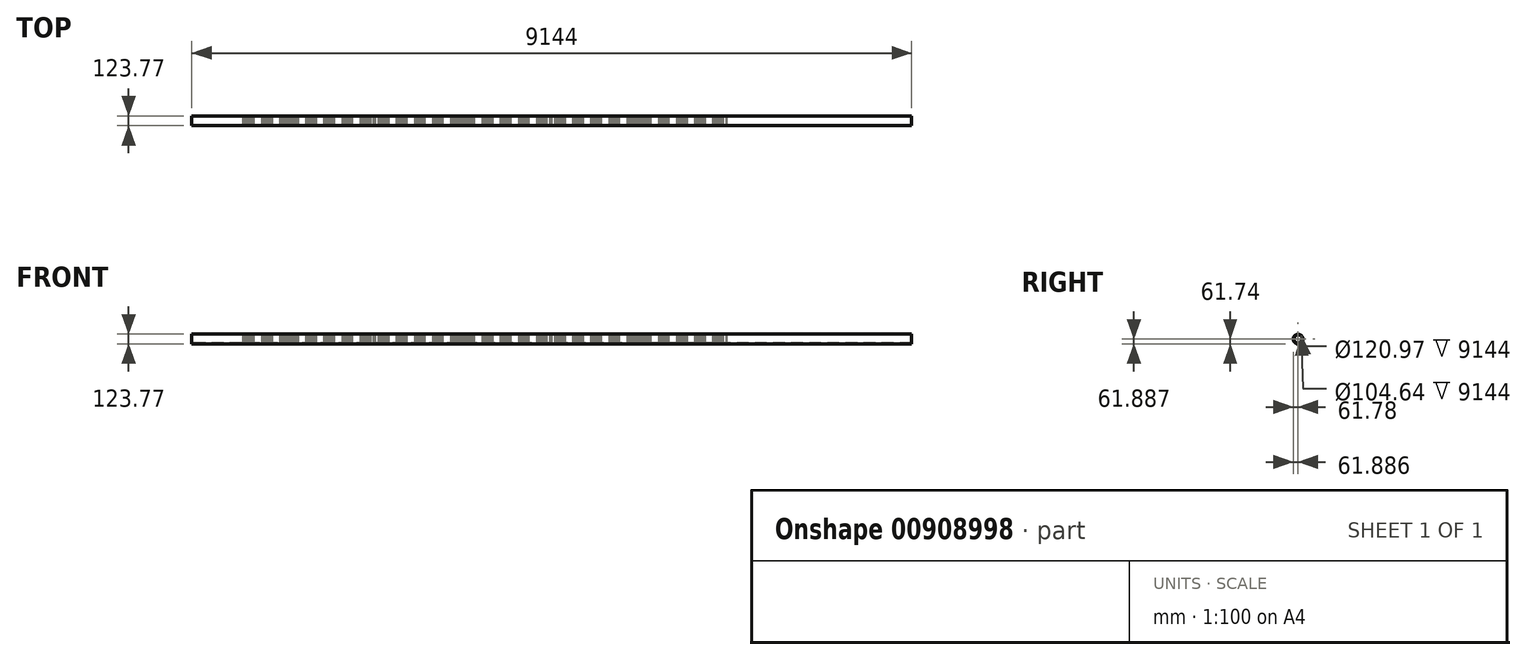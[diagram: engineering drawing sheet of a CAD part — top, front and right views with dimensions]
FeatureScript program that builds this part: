
annotation { "Feature Type Name" : "Feature", "Feature Type Description" : "" }
export const myFeature = defineFeature(function(context is Context, id is Id, definition is map)
    precondition{}
    {
        {
            var Q0;
            Q0=qCreatedBy(makeId("Right.planeOp"),FACE);
            var sketch = newSketch(context, id + "F0", { "sketchPlane" : qUnion([Q0])});
            skCircle(sketch, "E0", {"center": v(0, 0) * mm, "radius": 57.14 * mm});
            skCircle(sketch, "E1", {"center": v(0, 0) * mm, "radius": 52.32 * mm});
            skSolve(sketch);
        }
        {
            var Q0;
            Q0=qCreatedBy(makeId("Right.planeOp"),FACE);
            var sketch = newSketch(context, id + "F1", { "sketchPlane" : qUnion([Q0])});
            skLineSegment(sketch, "E2", {"start": v(57.25, 0) * mm, "end": v(57.25, 4.5) * mm});
            skLineSegment(sketch, "E3", {"start": v(57.25, 4.5) * mm, "end": v(59.26, 4.5) * mm});
            skLineSegment(sketch, "E4", {"start": v(59.26, 4.5) * mm, "end": v(59.26, -4.49) * mm});
            skLineSegment(sketch, "E5", {"start": v(59.26, -4.49) * mm, "end": v(57.25, -4.49) * mm});
            skLineSegment(sketch, "E6", {"start": v(57.25, -4.49) * mm, "end": v(57.25, 0) * mm});
            skSolve(sketch);
        }
        {
            var Q0;
            Q0=qCreatedBy(makeId("Front.planeOp"),FACE);
            var sketch = newSketch(context, id + "F2", { "sketchPlane" : qUnion([Q0])});
            skLineSegment(sketch, "E7", {"start": v(-71.44, 0) * mm, "end": v(74.71, 0) * mm, "construction": true});
            skSolve(sketch);
        }
        {
            var Q0;
            Q0 = qSketchRegion(id + "F0", true);
            extrude(context, id + "F3", {"entities" : qUnion([Q0]), "endBound" : BoundingType.SYMMETRIC, "depth" : 9144 * mm, "offsetDistance" : 25 * mm});
        }
        {
            var Q0;
            Q0 = qSketchRegion(id + "F1", true);
            extrude(context, id + "F4", {"entities" : qUnion([Q0]), "depth" : 1100 * mm, "offsetDistance" : 25 * mm});
        }
        {
            var Q0;
            Q0=makeQuery(id+"F4.opExtrude","SWEPT_BODY",BODY,{"disambiguationData":[OSD([sQuery(id+"F1.wireOp",EDGE,"E2"),sQuery(id+"F1.wireOp",EDGE,"E3"),sQuery(id+"F1.wireOp",EDGE,"E4"),sQuery(id+"F1.wireOp",EDGE,"E5"),sQuery(id+"F1.wireOp",EDGE,"E6")])]});
            var Q1;
            Q1=sQuery(id+"F2.wireOp",EDGE,"E7");
            circularPattern(context, id + "F5", {"entities" : qUnion([Q0]), "axis" : qUnion([Q1]), "angle" : 360 * degree, "instanceCount" : 36, "equalSpace" : true});
        }
        {
            var Q0;
            Q0=qCreatedBy(makeId("Front.planeOp"),FACE);
            var sketch = newSketch(context, id + "F6", { "sketchPlane" : qUnion([Q0])});
            skLineSegment(sketch, "E8", {"start": v(0, 0) * mm, "end": v(-199.98, 0) * mm, "construction": true});
            skSolve(sketch);
        }
        {
            var Q0;
            Q0=qCreatedBy(makeId("Right.planeOp"),FACE);
            cPlane(context, id + "F7", {"entities" : qUnion([Q0]), "cplaneType" : CPlaneType.OFFSET, "offset" : 10 * mm, "oppositeDirection" : true, "width" : 150 * mm, "height" : 150 * mm});
        }
        {
            var Q0;
            Q0=makeQuery(id+"F5.opPattern","COPY",BODY,{"derivedFrom":makeQuery(id+"F4.opExtrude","SWEPT_BODY",BODY,{"disambiguationData":[OSD([sQuery(id+"F1.wireOp",EDGE,"E2"),sQuery(id+"F1.wireOp",EDGE,"E3"),sQuery(id+"F1.wireOp",EDGE,"E4"),sQuery(id+"F1.wireOp",EDGE,"E5"),sQuery(id+"F1.wireOp",EDGE,"E6")])]}),"instanceName":"1"});
            var Q1;
            Q1=makeQuery(id+"F5.opPattern","COPY",BODY,{"derivedFrom":makeQuery(id+"F4.opExtrude","SWEPT_BODY",BODY,{"disambiguationData":[OSD([sQuery(id+"F1.wireOp",EDGE,"E2"),sQuery(id+"F1.wireOp",EDGE,"E3"),sQuery(id+"F1.wireOp",EDGE,"E4"),sQuery(id+"F1.wireOp",EDGE,"E5"),sQuery(id+"F1.wireOp",EDGE,"E6")])]}),"instanceName":"2"});
            var Q2;
            Q2=makeQuery(id+"F5.opPattern","COPY",BODY,{"derivedFrom":makeQuery(id+"F4.opExtrude","SWEPT_BODY",BODY,{"disambiguationData":[OSD([sQuery(id+"F1.wireOp",EDGE,"E2"),sQuery(id+"F1.wireOp",EDGE,"E3"),sQuery(id+"F1.wireOp",EDGE,"E4"),sQuery(id+"F1.wireOp",EDGE,"E5"),sQuery(id+"F1.wireOp",EDGE,"E6")])]}),"instanceName":"11"});
            var Q3;
            Q3=makeQuery(id+"F5.opPattern","COPY",BODY,{"derivedFrom":makeQuery(id+"F4.opExtrude","SWEPT_BODY",BODY,{"disambiguationData":[OSD([sQuery(id+"F1.wireOp",EDGE,"E2"),sQuery(id+"F1.wireOp",EDGE,"E3"),sQuery(id+"F1.wireOp",EDGE,"E4"),sQuery(id+"F1.wireOp",EDGE,"E5"),sQuery(id+"F1.wireOp",EDGE,"E6")])]}),"instanceName":"5"});
            var Q4;
            Q4=makeQuery(id+"F5.opPattern","COPY",BODY,{"derivedFrom":makeQuery(id+"F4.opExtrude","SWEPT_BODY",BODY,{"disambiguationData":[OSD([sQuery(id+"F1.wireOp",EDGE,"E2"),sQuery(id+"F1.wireOp",EDGE,"E3"),sQuery(id+"F1.wireOp",EDGE,"E4"),sQuery(id+"F1.wireOp",EDGE,"E5"),sQuery(id+"F1.wireOp",EDGE,"E6")])]}),"instanceName":"32"});
            var Q5;
            Q5=makeQuery(id+"F5.opPattern","COPY",BODY,{"derivedFrom":makeQuery(id+"F4.opExtrude","SWEPT_BODY",BODY,{"disambiguationData":[OSD([sQuery(id+"F1.wireOp",EDGE,"E2"),sQuery(id+"F1.wireOp",EDGE,"E3"),sQuery(id+"F1.wireOp",EDGE,"E4"),sQuery(id+"F1.wireOp",EDGE,"E5"),sQuery(id+"F1.wireOp",EDGE,"E6")])]}),"instanceName":"29"});
            var Q6;
            Q6=makeQuery(id+"F5.opPattern","COPY",BODY,{"derivedFrom":makeQuery(id+"F4.opExtrude","SWEPT_BODY",BODY,{"disambiguationData":[OSD([sQuery(id+"F1.wireOp",EDGE,"E2"),sQuery(id+"F1.wireOp",EDGE,"E3"),sQuery(id+"F1.wireOp",EDGE,"E4"),sQuery(id+"F1.wireOp",EDGE,"E5"),sQuery(id+"F1.wireOp",EDGE,"E6")])]}),"instanceName":"26"});
            var Q7;
            Q7=makeQuery(id+"F5.opPattern","COPY",BODY,{"derivedFrom":makeQuery(id+"F4.opExtrude","SWEPT_BODY",BODY,{"disambiguationData":[OSD([sQuery(id+"F1.wireOp",EDGE,"E2"),sQuery(id+"F1.wireOp",EDGE,"E3"),sQuery(id+"F1.wireOp",EDGE,"E4"),sQuery(id+"F1.wireOp",EDGE,"E5"),sQuery(id+"F1.wireOp",EDGE,"E6")])]}),"instanceName":"30"});
            var Q8;
            Q8=makeQuery(id+"F5.opPattern","COPY",BODY,{"derivedFrom":makeQuery(id+"F4.opExtrude","SWEPT_BODY",BODY,{"disambiguationData":[OSD([sQuery(id+"F1.wireOp",EDGE,"E2"),sQuery(id+"F1.wireOp",EDGE,"E3"),sQuery(id+"F1.wireOp",EDGE,"E4"),sQuery(id+"F1.wireOp",EDGE,"E5"),sQuery(id+"F1.wireOp",EDGE,"E6")])]}),"instanceName":"28"});
            var Q9;
            Q9=makeQuery(id+"F5.opPattern","COPY",BODY,{"derivedFrom":makeQuery(id+"F4.opExtrude","SWEPT_BODY",BODY,{"disambiguationData":[OSD([sQuery(id+"F1.wireOp",EDGE,"E2"),sQuery(id+"F1.wireOp",EDGE,"E3"),sQuery(id+"F1.wireOp",EDGE,"E4"),sQuery(id+"F1.wireOp",EDGE,"E5"),sQuery(id+"F1.wireOp",EDGE,"E6")])]}),"instanceName":"33"});
            var Q10;
            Q10=makeQuery(id+"F5.opPattern","COPY",BODY,{"derivedFrom":makeQuery(id+"F4.opExtrude","SWEPT_BODY",BODY,{"disambiguationData":[OSD([sQuery(id+"F1.wireOp",EDGE,"E2"),sQuery(id+"F1.wireOp",EDGE,"E3"),sQuery(id+"F1.wireOp",EDGE,"E4"),sQuery(id+"F1.wireOp",EDGE,"E5"),sQuery(id+"F1.wireOp",EDGE,"E6")])]}),"instanceName":"3"});
            var Q11;
            Q11=makeQuery(id+"F5.opPattern","COPY",BODY,{"derivedFrom":makeQuery(id+"F4.opExtrude","SWEPT_BODY",BODY,{"disambiguationData":[OSD([sQuery(id+"F1.wireOp",EDGE,"E2"),sQuery(id+"F1.wireOp",EDGE,"E3"),sQuery(id+"F1.wireOp",EDGE,"E4"),sQuery(id+"F1.wireOp",EDGE,"E5"),sQuery(id+"F1.wireOp",EDGE,"E6")])]}),"instanceName":"6"});
            var Q12;
            Q12=makeQuery(id+"F5.opPattern","COPY",BODY,{"derivedFrom":makeQuery(id+"F4.opExtrude","SWEPT_BODY",BODY,{"disambiguationData":[OSD([sQuery(id+"F1.wireOp",EDGE,"E2"),sQuery(id+"F1.wireOp",EDGE,"E3"),sQuery(id+"F1.wireOp",EDGE,"E4"),sQuery(id+"F1.wireOp",EDGE,"E5"),sQuery(id+"F1.wireOp",EDGE,"E6")])]}),"instanceName":"8"});
            var Q13;
            Q13=makeQuery(id+"F5.opPattern","COPY",BODY,{"derivedFrom":makeQuery(id+"F4.opExtrude","SWEPT_BODY",BODY,{"disambiguationData":[OSD([sQuery(id+"F1.wireOp",EDGE,"E2"),sQuery(id+"F1.wireOp",EDGE,"E3"),sQuery(id+"F1.wireOp",EDGE,"E4"),sQuery(id+"F1.wireOp",EDGE,"E5"),sQuery(id+"F1.wireOp",EDGE,"E6")])]}),"instanceName":"12"});
            var Q14;
            Q14=makeQuery(id+"F5.opPattern","COPY",BODY,{"derivedFrom":makeQuery(id+"F4.opExtrude","SWEPT_BODY",BODY,{"disambiguationData":[OSD([sQuery(id+"F1.wireOp",EDGE,"E2"),sQuery(id+"F1.wireOp",EDGE,"E3"),sQuery(id+"F1.wireOp",EDGE,"E4"),sQuery(id+"F1.wireOp",EDGE,"E5"),sQuery(id+"F1.wireOp",EDGE,"E6")])]}),"instanceName":"15"});
            var Q15;
            Q15=makeQuery(id+"F5.opPattern","COPY",BODY,{"derivedFrom":makeQuery(id+"F4.opExtrude","SWEPT_BODY",BODY,{"disambiguationData":[OSD([sQuery(id+"F1.wireOp",EDGE,"E2"),sQuery(id+"F1.wireOp",EDGE,"E3"),sQuery(id+"F1.wireOp",EDGE,"E4"),sQuery(id+"F1.wireOp",EDGE,"E5"),sQuery(id+"F1.wireOp",EDGE,"E6")])]}),"instanceName":"27"});
            var Q16;
            Q16=makeQuery(id+"F5.opPattern","COPY",BODY,{"derivedFrom":makeQuery(id+"F4.opExtrude","SWEPT_BODY",BODY,{"disambiguationData":[OSD([sQuery(id+"F1.wireOp",EDGE,"E2"),sQuery(id+"F1.wireOp",EDGE,"E3"),sQuery(id+"F1.wireOp",EDGE,"E4"),sQuery(id+"F1.wireOp",EDGE,"E5"),sQuery(id+"F1.wireOp",EDGE,"E6")])]}),"instanceName":"31"});
            var Q17;
            Q17=makeQuery(id+"F5.opPattern","COPY",BODY,{"derivedFrom":makeQuery(id+"F4.opExtrude","SWEPT_BODY",BODY,{"disambiguationData":[OSD([sQuery(id+"F1.wireOp",EDGE,"E2"),sQuery(id+"F1.wireOp",EDGE,"E3"),sQuery(id+"F1.wireOp",EDGE,"E4"),sQuery(id+"F1.wireOp",EDGE,"E5"),sQuery(id+"F1.wireOp",EDGE,"E6")])]}),"instanceName":"13"});
            var Q18;
            Q18=makeQuery(id+"F5.opPattern","COPY",BODY,{"derivedFrom":makeQuery(id+"F4.opExtrude","SWEPT_BODY",BODY,{"disambiguationData":[OSD([sQuery(id+"F1.wireOp",EDGE,"E2"),sQuery(id+"F1.wireOp",EDGE,"E3"),sQuery(id+"F1.wireOp",EDGE,"E4"),sQuery(id+"F1.wireOp",EDGE,"E5"),sQuery(id+"F1.wireOp",EDGE,"E6")])]}),"instanceName":"9"});
            var Q19;
            Q19=makeQuery(id+"F5.opPattern","COPY",BODY,{"derivedFrom":makeQuery(id+"F4.opExtrude","SWEPT_BODY",BODY,{"disambiguationData":[OSD([sQuery(id+"F1.wireOp",EDGE,"E2"),sQuery(id+"F1.wireOp",EDGE,"E3"),sQuery(id+"F1.wireOp",EDGE,"E4"),sQuery(id+"F1.wireOp",EDGE,"E5"),sQuery(id+"F1.wireOp",EDGE,"E6")])]}),"instanceName":"4"});
            var Q20;
            Q20=makeQuery(id+"F5.opPattern","COPY",BODY,{"derivedFrom":makeQuery(id+"F4.opExtrude","SWEPT_BODY",BODY,{"disambiguationData":[OSD([sQuery(id+"F1.wireOp",EDGE,"E2"),sQuery(id+"F1.wireOp",EDGE,"E3"),sQuery(id+"F1.wireOp",EDGE,"E4"),sQuery(id+"F1.wireOp",EDGE,"E5"),sQuery(id+"F1.wireOp",EDGE,"E6")])]}),"instanceName":"7"});
            var Q21;
            Q21=makeQuery(id+"F5.opPattern","COPY",BODY,{"derivedFrom":makeQuery(id+"F4.opExtrude","SWEPT_BODY",BODY,{"disambiguationData":[OSD([sQuery(id+"F1.wireOp",EDGE,"E2"),sQuery(id+"F1.wireOp",EDGE,"E3"),sQuery(id+"F1.wireOp",EDGE,"E4"),sQuery(id+"F1.wireOp",EDGE,"E5"),sQuery(id+"F1.wireOp",EDGE,"E6")])]}),"instanceName":"10"});
            var Q22;
            Q22=makeQuery(id+"F5.opPattern","COPY",BODY,{"derivedFrom":makeQuery(id+"F4.opExtrude","SWEPT_BODY",BODY,{"disambiguationData":[OSD([sQuery(id+"F1.wireOp",EDGE,"E2"),sQuery(id+"F1.wireOp",EDGE,"E3"),sQuery(id+"F1.wireOp",EDGE,"E4"),sQuery(id+"F1.wireOp",EDGE,"E5"),sQuery(id+"F1.wireOp",EDGE,"E6")])]}),"instanceName":"34"});
            var Q23;
            Q23=makeQuery(id+"F5.opPattern","COPY",BODY,{"derivedFrom":makeQuery(id+"F4.opExtrude","SWEPT_BODY",BODY,{"disambiguationData":[OSD([sQuery(id+"F1.wireOp",EDGE,"E2"),sQuery(id+"F1.wireOp",EDGE,"E3"),sQuery(id+"F1.wireOp",EDGE,"E4"),sQuery(id+"F1.wireOp",EDGE,"E5"),sQuery(id+"F1.wireOp",EDGE,"E6")])]}),"instanceName":"35"});
            var Q24;
            Q24=makeQuery(id+"F5.opPattern","COPY",BODY,{"derivedFrom":makeQuery(id+"F4.opExtrude","SWEPT_BODY",BODY,{"disambiguationData":[OSD([sQuery(id+"F1.wireOp",EDGE,"E2"),sQuery(id+"F1.wireOp",EDGE,"E3"),sQuery(id+"F1.wireOp",EDGE,"E4"),sQuery(id+"F1.wireOp",EDGE,"E5"),sQuery(id+"F1.wireOp",EDGE,"E6")])]}),"instanceName":"19"});
            var Q25;
            Q25=makeQuery(id+"F5.opPattern","COPY",BODY,{"derivedFrom":makeQuery(id+"F4.opExtrude","SWEPT_BODY",BODY,{"disambiguationData":[OSD([sQuery(id+"F1.wireOp",EDGE,"E2"),sQuery(id+"F1.wireOp",EDGE,"E3"),sQuery(id+"F1.wireOp",EDGE,"E4"),sQuery(id+"F1.wireOp",EDGE,"E5"),sQuery(id+"F1.wireOp",EDGE,"E6")])]}),"instanceName":"21"});
            var Q26;
            Q26=makeQuery(id+"F5.opPattern","COPY",BODY,{"derivedFrom":makeQuery(id+"F4.opExtrude","SWEPT_BODY",BODY,{"disambiguationData":[OSD([sQuery(id+"F1.wireOp",EDGE,"E2"),sQuery(id+"F1.wireOp",EDGE,"E3"),sQuery(id+"F1.wireOp",EDGE,"E4"),sQuery(id+"F1.wireOp",EDGE,"E5"),sQuery(id+"F1.wireOp",EDGE,"E6")])]}),"instanceName":"23"});
            var Q27;
            Q27=makeQuery(id+"F5.opPattern","COPY",BODY,{"derivedFrom":makeQuery(id+"F4.opExtrude","SWEPT_BODY",BODY,{"disambiguationData":[OSD([sQuery(id+"F1.wireOp",EDGE,"E2"),sQuery(id+"F1.wireOp",EDGE,"E3"),sQuery(id+"F1.wireOp",EDGE,"E4"),sQuery(id+"F1.wireOp",EDGE,"E5"),sQuery(id+"F1.wireOp",EDGE,"E6")])]}),"instanceName":"17"});
            var Q28;
            Q28=makeQuery(id+"F5.opPattern","COPY",BODY,{"derivedFrom":makeQuery(id+"F4.opExtrude","SWEPT_BODY",BODY,{"disambiguationData":[OSD([sQuery(id+"F1.wireOp",EDGE,"E2"),sQuery(id+"F1.wireOp",EDGE,"E3"),sQuery(id+"F1.wireOp",EDGE,"E4"),sQuery(id+"F1.wireOp",EDGE,"E5"),sQuery(id+"F1.wireOp",EDGE,"E6")])]}),"instanceName":"14"});
            var Q29;
            Q29=makeQuery(id+"F4.opExtrude","SWEPT_BODY",BODY,{"disambiguationData":[OSD([sQuery(id+"F1.wireOp",EDGE,"E2"),sQuery(id+"F1.wireOp",EDGE,"E3"),sQuery(id+"F1.wireOp",EDGE,"E4"),sQuery(id+"F1.wireOp",EDGE,"E5"),sQuery(id+"F1.wireOp",EDGE,"E6")])]});
            var Q30;
            Q30=makeQuery(id+"F5.opPattern","COPY",BODY,{"derivedFrom":makeQuery(id+"F4.opExtrude","SWEPT_BODY",BODY,{"disambiguationData":[OSD([sQuery(id+"F1.wireOp",EDGE,"E2"),sQuery(id+"F1.wireOp",EDGE,"E3"),sQuery(id+"F1.wireOp",EDGE,"E4"),sQuery(id+"F1.wireOp",EDGE,"E5"),sQuery(id+"F1.wireOp",EDGE,"E6")])]}),"instanceName":"18"});
            var Q31;
            Q31=makeQuery(id+"F5.opPattern","COPY",BODY,{"derivedFrom":makeQuery(id+"F4.opExtrude","SWEPT_BODY",BODY,{"disambiguationData":[OSD([sQuery(id+"F1.wireOp",EDGE,"E2"),sQuery(id+"F1.wireOp",EDGE,"E3"),sQuery(id+"F1.wireOp",EDGE,"E4"),sQuery(id+"F1.wireOp",EDGE,"E5"),sQuery(id+"F1.wireOp",EDGE,"E6")])]}),"instanceName":"20"});
            var Q32;
            Q32=makeQuery(id+"F5.opPattern","COPY",BODY,{"derivedFrom":makeQuery(id+"F4.opExtrude","SWEPT_BODY",BODY,{"disambiguationData":[OSD([sQuery(id+"F1.wireOp",EDGE,"E2"),sQuery(id+"F1.wireOp",EDGE,"E3"),sQuery(id+"F1.wireOp",EDGE,"E4"),sQuery(id+"F1.wireOp",EDGE,"E5"),sQuery(id+"F1.wireOp",EDGE,"E6")])]}),"instanceName":"22"});
            var Q33;
            Q33=makeQuery(id+"F5.opPattern","COPY",BODY,{"derivedFrom":makeQuery(id+"F4.opExtrude","SWEPT_BODY",BODY,{"disambiguationData":[OSD([sQuery(id+"F1.wireOp",EDGE,"E2"),sQuery(id+"F1.wireOp",EDGE,"E3"),sQuery(id+"F1.wireOp",EDGE,"E4"),sQuery(id+"F1.wireOp",EDGE,"E5"),sQuery(id+"F1.wireOp",EDGE,"E6")])]}),"instanceName":"24"});
            var Q34;
            Q34=makeQuery(id+"F5.opPattern","COPY",BODY,{"derivedFrom":makeQuery(id+"F4.opExtrude","SWEPT_BODY",BODY,{"disambiguationData":[OSD([sQuery(id+"F1.wireOp",EDGE,"E2"),sQuery(id+"F1.wireOp",EDGE,"E3"),sQuery(id+"F1.wireOp",EDGE,"E4"),sQuery(id+"F1.wireOp",EDGE,"E5"),sQuery(id+"F1.wireOp",EDGE,"E6")])]}),"instanceName":"25"});
            var Q35;
            Q35=makeQuery(id+"F5.opPattern","COPY",BODY,{"derivedFrom":makeQuery(id+"F4.opExtrude","SWEPT_BODY",BODY,{"disambiguationData":[OSD([sQuery(id+"F1.wireOp",EDGE,"E2"),sQuery(id+"F1.wireOp",EDGE,"E3"),sQuery(id+"F1.wireOp",EDGE,"E4"),sQuery(id+"F1.wireOp",EDGE,"E5"),sQuery(id+"F1.wireOp",EDGE,"E6")])]}),"instanceName":"16"});
            var Q36;
            Q36=qCreatedBy(id+"F7.planeOp",FACE);
            mirror(context, id + "F8", {"entities" : qUnion([Q0, Q1, Q2, Q3, Q4, Q5, Q6, Q7, Q8, Q9, Q10, Q11, Q12, Q13, Q14, Q15, Q16, Q17, Q18, Q19, Q20, Q21, Q22, Q23, Q24, Q25, Q26, Q27, Q28, Q29, Q30, Q31, Q32, Q33, Q34, Q35]), "mirrorPlane" : qUnion([Q36])});
        }
        {
            var Q0;
            Q0=qCreatedBy(makeId("Right.planeOp"),FACE);
            var Q1;
            Q1=makeQuery(id+"F5.opPattern","COPY",VERTEX,{"derivedFrom":makeQuery(id+"F4.opExtrude","CAP_VERTEX",VERTEX,{"disambiguationData":[OSD([sQuery(id+"F1.wireOp",EDGE,"E2"),sQuery(id+"F1.wireOp",EDGE,"E6")])],"isStart":false}),"instanceName":"11"});
            cPlane(context, id + "F9", {"entities" : qUnion([Q0, Q1]), "cplaneType" : CPlaneType.PLANE_POINT, "offset" : 25 * mm, "width" : 150 * mm, "height" : 150 * mm});
        }
        {
            var Q0;
            Q0=qCreatedBy(id+"F9.planeOp",FACE);
            cPlane(context, id + "F10", {"entities" : qUnion([Q0]), "cplaneType" : CPlaneType.OFFSET, "offset" : 10 * mm, "width" : 150 * mm, "height" : 150 * mm});
        }
        {
            var Q0;
            Q0=makeQuery(id+"F5.opPattern","COPY",BODY,{"derivedFrom":makeQuery(id+"F4.opExtrude","SWEPT_BODY",BODY,{"disambiguationData":[OSD([sQuery(id+"F1.wireOp",EDGE,"E2"),sQuery(id+"F1.wireOp",EDGE,"E3"),sQuery(id+"F1.wireOp",EDGE,"E4"),sQuery(id+"F1.wireOp",EDGE,"E5"),sQuery(id+"F1.wireOp",EDGE,"E6")])]}),"instanceName":"1"});
            var Q1;
            Q1=makeQuery(id+"F5.opPattern","COPY",BODY,{"derivedFrom":makeQuery(id+"F4.opExtrude","SWEPT_BODY",BODY,{"disambiguationData":[OSD([sQuery(id+"F1.wireOp",EDGE,"E2"),sQuery(id+"F1.wireOp",EDGE,"E3"),sQuery(id+"F1.wireOp",EDGE,"E4"),sQuery(id+"F1.wireOp",EDGE,"E5"),sQuery(id+"F1.wireOp",EDGE,"E6")])]}),"instanceName":"2"});
            var Q2;
            Q2=makeQuery(id+"F5.opPattern","COPY",BODY,{"derivedFrom":makeQuery(id+"F4.opExtrude","SWEPT_BODY",BODY,{"disambiguationData":[OSD([sQuery(id+"F1.wireOp",EDGE,"E2"),sQuery(id+"F1.wireOp",EDGE,"E3"),sQuery(id+"F1.wireOp",EDGE,"E4"),sQuery(id+"F1.wireOp",EDGE,"E5"),sQuery(id+"F1.wireOp",EDGE,"E6")])]}),"instanceName":"5"});
            var Q3;
            Q3=makeQuery(id+"F4.opExtrude","SWEPT_BODY",BODY,{"disambiguationData":[OSD([sQuery(id+"F1.wireOp",EDGE,"E2"),sQuery(id+"F1.wireOp",EDGE,"E3"),sQuery(id+"F1.wireOp",EDGE,"E4"),sQuery(id+"F1.wireOp",EDGE,"E5"),sQuery(id+"F1.wireOp",EDGE,"E6")])]});
            var Q4;
            Q4=makeQuery(id+"F5.opPattern","COPY",BODY,{"derivedFrom":makeQuery(id+"F4.opExtrude","SWEPT_BODY",BODY,{"disambiguationData":[OSD([sQuery(id+"F1.wireOp",EDGE,"E2"),sQuery(id+"F1.wireOp",EDGE,"E3"),sQuery(id+"F1.wireOp",EDGE,"E4"),sQuery(id+"F1.wireOp",EDGE,"E5"),sQuery(id+"F1.wireOp",EDGE,"E6")])]}),"instanceName":"32"});
            var Q5;
            Q5=makeQuery(id+"F5.opPattern","COPY",BODY,{"derivedFrom":makeQuery(id+"F4.opExtrude","SWEPT_BODY",BODY,{"disambiguationData":[OSD([sQuery(id+"F1.wireOp",EDGE,"E2"),sQuery(id+"F1.wireOp",EDGE,"E3"),sQuery(id+"F1.wireOp",EDGE,"E4"),sQuery(id+"F1.wireOp",EDGE,"E5"),sQuery(id+"F1.wireOp",EDGE,"E6")])]}),"instanceName":"33"});
            var Q6;
            Q6=makeQuery(id+"F5.opPattern","COPY",BODY,{"derivedFrom":makeQuery(id+"F4.opExtrude","SWEPT_BODY",BODY,{"disambiguationData":[OSD([sQuery(id+"F1.wireOp",EDGE,"E2"),sQuery(id+"F1.wireOp",EDGE,"E3"),sQuery(id+"F1.wireOp",EDGE,"E4"),sQuery(id+"F1.wireOp",EDGE,"E5"),sQuery(id+"F1.wireOp",EDGE,"E6")])]}),"instanceName":"3"});
            var Q7;
            Q7=makeQuery(id+"F5.opPattern","COPY",BODY,{"derivedFrom":makeQuery(id+"F4.opExtrude","SWEPT_BODY",BODY,{"disambiguationData":[OSD([sQuery(id+"F1.wireOp",EDGE,"E2"),sQuery(id+"F1.wireOp",EDGE,"E3"),sQuery(id+"F1.wireOp",EDGE,"E4"),sQuery(id+"F1.wireOp",EDGE,"E5"),sQuery(id+"F1.wireOp",EDGE,"E6")])]}),"instanceName":"18"});
            var Q8;
            Q8=makeQuery(id+"F5.opPattern","COPY",BODY,{"derivedFrom":makeQuery(id+"F4.opExtrude","SWEPT_BODY",BODY,{"disambiguationData":[OSD([sQuery(id+"F1.wireOp",EDGE,"E2"),sQuery(id+"F1.wireOp",EDGE,"E3"),sQuery(id+"F1.wireOp",EDGE,"E4"),sQuery(id+"F1.wireOp",EDGE,"E5"),sQuery(id+"F1.wireOp",EDGE,"E6")])]}),"instanceName":"34"});
            var Q9;
            Q9=makeQuery(id+"F5.opPattern","COPY",BODY,{"derivedFrom":makeQuery(id+"F4.opExtrude","SWEPT_BODY",BODY,{"disambiguationData":[OSD([sQuery(id+"F1.wireOp",EDGE,"E2"),sQuery(id+"F1.wireOp",EDGE,"E3"),sQuery(id+"F1.wireOp",EDGE,"E4"),sQuery(id+"F1.wireOp",EDGE,"E5"),sQuery(id+"F1.wireOp",EDGE,"E6")])]}),"instanceName":"35"});
            var Q10;
            Q10=makeQuery(id+"F5.opPattern","COPY",BODY,{"derivedFrom":makeQuery(id+"F4.opExtrude","SWEPT_BODY",BODY,{"disambiguationData":[OSD([sQuery(id+"F1.wireOp",EDGE,"E2"),sQuery(id+"F1.wireOp",EDGE,"E3"),sQuery(id+"F1.wireOp",EDGE,"E4"),sQuery(id+"F1.wireOp",EDGE,"E5"),sQuery(id+"F1.wireOp",EDGE,"E6")])]}),"instanceName":"19"});
            var Q11;
            Q11=makeQuery(id+"F5.opPattern","COPY",BODY,{"derivedFrom":makeQuery(id+"F4.opExtrude","SWEPT_BODY",BODY,{"disambiguationData":[OSD([sQuery(id+"F1.wireOp",EDGE,"E2"),sQuery(id+"F1.wireOp",EDGE,"E3"),sQuery(id+"F1.wireOp",EDGE,"E4"),sQuery(id+"F1.wireOp",EDGE,"E5"),sQuery(id+"F1.wireOp",EDGE,"E6")])]}),"instanceName":"21"});
            var Q12;
            Q12=makeQuery(id+"F5.opPattern","COPY",BODY,{"derivedFrom":makeQuery(id+"F4.opExtrude","SWEPT_BODY",BODY,{"disambiguationData":[OSD([sQuery(id+"F1.wireOp",EDGE,"E2"),sQuery(id+"F1.wireOp",EDGE,"E3"),sQuery(id+"F1.wireOp",EDGE,"E4"),sQuery(id+"F1.wireOp",EDGE,"E5"),sQuery(id+"F1.wireOp",EDGE,"E6")])]}),"instanceName":"17"});
            var Q13;
            Q13=makeQuery(id+"F5.opPattern","COPY",BODY,{"derivedFrom":makeQuery(id+"F4.opExtrude","SWEPT_BODY",BODY,{"disambiguationData":[OSD([sQuery(id+"F1.wireOp",EDGE,"E2"),sQuery(id+"F1.wireOp",EDGE,"E3"),sQuery(id+"F1.wireOp",EDGE,"E4"),sQuery(id+"F1.wireOp",EDGE,"E5"),sQuery(id+"F1.wireOp",EDGE,"E6")])]}),"instanceName":"14"});
            var Q14;
            Q14=makeQuery(id+"F5.opPattern","COPY",BODY,{"derivedFrom":makeQuery(id+"F4.opExtrude","SWEPT_BODY",BODY,{"disambiguationData":[OSD([sQuery(id+"F1.wireOp",EDGE,"E2"),sQuery(id+"F1.wireOp",EDGE,"E3"),sQuery(id+"F1.wireOp",EDGE,"E4"),sQuery(id+"F1.wireOp",EDGE,"E5"),sQuery(id+"F1.wireOp",EDGE,"E6")])]}),"instanceName":"30"});
            var Q15;
            Q15=makeQuery(id+"F5.opPattern","COPY",BODY,{"derivedFrom":makeQuery(id+"F4.opExtrude","SWEPT_BODY",BODY,{"disambiguationData":[OSD([sQuery(id+"F1.wireOp",EDGE,"E2"),sQuery(id+"F1.wireOp",EDGE,"E3"),sQuery(id+"F1.wireOp",EDGE,"E4"),sQuery(id+"F1.wireOp",EDGE,"E5"),sQuery(id+"F1.wireOp",EDGE,"E6")])]}),"instanceName":"15"});
            var Q16;
            Q16=makeQuery(id+"F5.opPattern","COPY",BODY,{"derivedFrom":makeQuery(id+"F4.opExtrude","SWEPT_BODY",BODY,{"disambiguationData":[OSD([sQuery(id+"F1.wireOp",EDGE,"E2"),sQuery(id+"F1.wireOp",EDGE,"E3"),sQuery(id+"F1.wireOp",EDGE,"E4"),sQuery(id+"F1.wireOp",EDGE,"E5"),sQuery(id+"F1.wireOp",EDGE,"E6")])]}),"instanceName":"20"});
            var Q17;
            Q17=makeQuery(id+"F5.opPattern","COPY",BODY,{"derivedFrom":makeQuery(id+"F4.opExtrude","SWEPT_BODY",BODY,{"disambiguationData":[OSD([sQuery(id+"F1.wireOp",EDGE,"E2"),sQuery(id+"F1.wireOp",EDGE,"E3"),sQuery(id+"F1.wireOp",EDGE,"E4"),sQuery(id+"F1.wireOp",EDGE,"E5"),sQuery(id+"F1.wireOp",EDGE,"E6")])]}),"instanceName":"31"});
            var Q18;
            Q18=makeQuery(id+"F5.opPattern","COPY",BODY,{"derivedFrom":makeQuery(id+"F4.opExtrude","SWEPT_BODY",BODY,{"disambiguationData":[OSD([sQuery(id+"F1.wireOp",EDGE,"E2"),sQuery(id+"F1.wireOp",EDGE,"E3"),sQuery(id+"F1.wireOp",EDGE,"E4"),sQuery(id+"F1.wireOp",EDGE,"E5"),sQuery(id+"F1.wireOp",EDGE,"E6")])]}),"instanceName":"13"});
            var Q19;
            Q19=makeQuery(id+"F5.opPattern","COPY",BODY,{"derivedFrom":makeQuery(id+"F4.opExtrude","SWEPT_BODY",BODY,{"disambiguationData":[OSD([sQuery(id+"F1.wireOp",EDGE,"E2"),sQuery(id+"F1.wireOp",EDGE,"E3"),sQuery(id+"F1.wireOp",EDGE,"E4"),sQuery(id+"F1.wireOp",EDGE,"E5"),sQuery(id+"F1.wireOp",EDGE,"E6")])]}),"instanceName":"16"});
            var Q20;
            Q20=makeQuery(id+"F5.opPattern","COPY",BODY,{"derivedFrom":makeQuery(id+"F4.opExtrude","SWEPT_BODY",BODY,{"disambiguationData":[OSD([sQuery(id+"F1.wireOp",EDGE,"E2"),sQuery(id+"F1.wireOp",EDGE,"E3"),sQuery(id+"F1.wireOp",EDGE,"E4"),sQuery(id+"F1.wireOp",EDGE,"E5"),sQuery(id+"F1.wireOp",EDGE,"E6")])]}),"instanceName":"4"});
            var Q21;
            Q21=makeQuery(id+"F5.opPattern","COPY",BODY,{"derivedFrom":makeQuery(id+"F4.opExtrude","SWEPT_BODY",BODY,{"disambiguationData":[OSD([sQuery(id+"F1.wireOp",EDGE,"E2"),sQuery(id+"F1.wireOp",EDGE,"E3"),sQuery(id+"F1.wireOp",EDGE,"E4"),sQuery(id+"F1.wireOp",EDGE,"E5"),sQuery(id+"F1.wireOp",EDGE,"E6")])]}),"instanceName":"23"});
            var Q22;
            Q22=makeQuery(id+"F5.opPattern","COPY",BODY,{"derivedFrom":makeQuery(id+"F4.opExtrude","SWEPT_BODY",BODY,{"disambiguationData":[OSD([sQuery(id+"F1.wireOp",EDGE,"E2"),sQuery(id+"F1.wireOp",EDGE,"E3"),sQuery(id+"F1.wireOp",EDGE,"E4"),sQuery(id+"F1.wireOp",EDGE,"E5"),sQuery(id+"F1.wireOp",EDGE,"E6")])]}),"instanceName":"29"});
            var Q23;
            Q23=makeQuery(id+"F5.opPattern","COPY",BODY,{"derivedFrom":makeQuery(id+"F4.opExtrude","SWEPT_BODY",BODY,{"disambiguationData":[OSD([sQuery(id+"F1.wireOp",EDGE,"E2"),sQuery(id+"F1.wireOp",EDGE,"E3"),sQuery(id+"F1.wireOp",EDGE,"E4"),sQuery(id+"F1.wireOp",EDGE,"E5"),sQuery(id+"F1.wireOp",EDGE,"E6")])]}),"instanceName":"6"});
            var Q24;
            Q24=makeQuery(id+"F5.opPattern","COPY",BODY,{"derivedFrom":makeQuery(id+"F4.opExtrude","SWEPT_BODY",BODY,{"disambiguationData":[OSD([sQuery(id+"F1.wireOp",EDGE,"E2"),sQuery(id+"F1.wireOp",EDGE,"E3"),sQuery(id+"F1.wireOp",EDGE,"E4"),sQuery(id+"F1.wireOp",EDGE,"E5"),sQuery(id+"F1.wireOp",EDGE,"E6")])]}),"instanceName":"22"});
            var Q25;
            Q25=makeQuery(id+"F5.opPattern","COPY",BODY,{"derivedFrom":makeQuery(id+"F4.opExtrude","SWEPT_BODY",BODY,{"disambiguationData":[OSD([sQuery(id+"F1.wireOp",EDGE,"E2"),sQuery(id+"F1.wireOp",EDGE,"E3"),sQuery(id+"F1.wireOp",EDGE,"E4"),sQuery(id+"F1.wireOp",EDGE,"E5"),sQuery(id+"F1.wireOp",EDGE,"E6")])]}),"instanceName":"11"});
            var Q26;
            Q26=makeQuery(id+"F5.opPattern","COPY",BODY,{"derivedFrom":makeQuery(id+"F4.opExtrude","SWEPT_BODY",BODY,{"disambiguationData":[OSD([sQuery(id+"F1.wireOp",EDGE,"E2"),sQuery(id+"F1.wireOp",EDGE,"E3"),sQuery(id+"F1.wireOp",EDGE,"E4"),sQuery(id+"F1.wireOp",EDGE,"E5"),sQuery(id+"F1.wireOp",EDGE,"E6")])]}),"instanceName":"28"});
            var Q27;
            Q27=makeQuery(id+"F5.opPattern","COPY",BODY,{"derivedFrom":makeQuery(id+"F4.opExtrude","SWEPT_BODY",BODY,{"disambiguationData":[OSD([sQuery(id+"F1.wireOp",EDGE,"E2"),sQuery(id+"F1.wireOp",EDGE,"E3"),sQuery(id+"F1.wireOp",EDGE,"E4"),sQuery(id+"F1.wireOp",EDGE,"E5"),sQuery(id+"F1.wireOp",EDGE,"E6")])]}),"instanceName":"12"});
            var Q28;
            Q28=makeQuery(id+"F5.opPattern","COPY",BODY,{"derivedFrom":makeQuery(id+"F4.opExtrude","SWEPT_BODY",BODY,{"disambiguationData":[OSD([sQuery(id+"F1.wireOp",EDGE,"E2"),sQuery(id+"F1.wireOp",EDGE,"E3"),sQuery(id+"F1.wireOp",EDGE,"E4"),sQuery(id+"F1.wireOp",EDGE,"E5"),sQuery(id+"F1.wireOp",EDGE,"E6")])]}),"instanceName":"24"});
            var Q29;
            Q29=makeQuery(id+"F5.opPattern","COPY",BODY,{"derivedFrom":makeQuery(id+"F4.opExtrude","SWEPT_BODY",BODY,{"disambiguationData":[OSD([sQuery(id+"F1.wireOp",EDGE,"E2"),sQuery(id+"F1.wireOp",EDGE,"E3"),sQuery(id+"F1.wireOp",EDGE,"E4"),sQuery(id+"F1.wireOp",EDGE,"E5"),sQuery(id+"F1.wireOp",EDGE,"E6")])]}),"instanceName":"7"});
            var Q30;
            Q30=makeQuery(id+"F5.opPattern","COPY",BODY,{"derivedFrom":makeQuery(id+"F4.opExtrude","SWEPT_BODY",BODY,{"disambiguationData":[OSD([sQuery(id+"F1.wireOp",EDGE,"E2"),sQuery(id+"F1.wireOp",EDGE,"E3"),sQuery(id+"F1.wireOp",EDGE,"E4"),sQuery(id+"F1.wireOp",EDGE,"E5"),sQuery(id+"F1.wireOp",EDGE,"E6")])]}),"instanceName":"27"});
            var Q31;
            Q31=makeQuery(id+"F5.opPattern","COPY",BODY,{"derivedFrom":makeQuery(id+"F4.opExtrude","SWEPT_BODY",BODY,{"disambiguationData":[OSD([sQuery(id+"F1.wireOp",EDGE,"E2"),sQuery(id+"F1.wireOp",EDGE,"E3"),sQuery(id+"F1.wireOp",EDGE,"E4"),sQuery(id+"F1.wireOp",EDGE,"E5"),sQuery(id+"F1.wireOp",EDGE,"E6")])]}),"instanceName":"10"});
            var Q32;
            Q32=makeQuery(id+"F5.opPattern","COPY",BODY,{"derivedFrom":makeQuery(id+"F4.opExtrude","SWEPT_BODY",BODY,{"disambiguationData":[OSD([sQuery(id+"F1.wireOp",EDGE,"E2"),sQuery(id+"F1.wireOp",EDGE,"E3"),sQuery(id+"F1.wireOp",EDGE,"E4"),sQuery(id+"F1.wireOp",EDGE,"E5"),sQuery(id+"F1.wireOp",EDGE,"E6")])]}),"instanceName":"25"});
            var Q33;
            Q33=makeQuery(id+"F5.opPattern","COPY",BODY,{"derivedFrom":makeQuery(id+"F4.opExtrude","SWEPT_BODY",BODY,{"disambiguationData":[OSD([sQuery(id+"F1.wireOp",EDGE,"E2"),sQuery(id+"F1.wireOp",EDGE,"E3"),sQuery(id+"F1.wireOp",EDGE,"E4"),sQuery(id+"F1.wireOp",EDGE,"E5"),sQuery(id+"F1.wireOp",EDGE,"E6")])]}),"instanceName":"8"});
            var Q34;
            Q34=makeQuery(id+"F5.opPattern","COPY",BODY,{"derivedFrom":makeQuery(id+"F4.opExtrude","SWEPT_BODY",BODY,{"disambiguationData":[OSD([sQuery(id+"F1.wireOp",EDGE,"E2"),sQuery(id+"F1.wireOp",EDGE,"E3"),sQuery(id+"F1.wireOp",EDGE,"E4"),sQuery(id+"F1.wireOp",EDGE,"E5"),sQuery(id+"F1.wireOp",EDGE,"E6")])]}),"instanceName":"26"});
            var Q35;
            Q35=makeQuery(id+"F5.opPattern","COPY",BODY,{"derivedFrom":makeQuery(id+"F4.opExtrude","SWEPT_BODY",BODY,{"disambiguationData":[OSD([sQuery(id+"F1.wireOp",EDGE,"E2"),sQuery(id+"F1.wireOp",EDGE,"E3"),sQuery(id+"F1.wireOp",EDGE,"E4"),sQuery(id+"F1.wireOp",EDGE,"E5"),sQuery(id+"F1.wireOp",EDGE,"E6")])]}),"instanceName":"9"});
            var Q36;
            Q36=qCreatedBy(id+"F10.planeOp",FACE);
            mirror(context, id + "F11", {"entities" : qUnion([Q0, Q1, Q2, Q3, Q4, Q5, Q6, Q7, Q8, Q9, Q10, Q11, Q12, Q13, Q14, Q15, Q16, Q17, Q18, Q19, Q20, Q21, Q22, Q23, Q24, Q25, Q26, Q27, Q28, Q29, Q30, Q31, Q32, Q33, Q34, Q35]), "mirrorPlane" : qUnion([Q36])});
        }
        {
            var Q0;
            Q0=qCreatedBy(makeId("Right.planeOp"),FACE);
            var Q1;
            Q1=makeQuery(id+"F8.opPattern","COPY",VERTEX,{"derivedFrom":makeQuery(id+"F5.opPattern","COPY",VERTEX,{"derivedFrom":makeQuery(id+"F4.opExtrude","CAP_VERTEX",VERTEX,{"disambiguationData":[OSD([sQuery(id+"F1.wireOp",EDGE,"E5"),sQuery(id+"F1.wireOp",EDGE,"E6")])],"isStart":false}),"instanceName":"11"}),"instanceName":"1"});
            cPlane(context, id + "F12", {"entities" : qUnion([Q0, Q1]), "cplaneType" : CPlaneType.PLANE_POINT, "offset" : 25 * mm, "width" : 150 * mm, "height" : 150 * mm});
        }
        {
            var Q0;
            Q0=qCreatedBy(id+"F12.planeOp",FACE);
            cPlane(context, id + "F13", {"entities" : qUnion([Q0]), "cplaneType" : CPlaneType.OFFSET, "offset" : 10 * mm, "oppositeDirection" : true, "width" : 150 * mm, "height" : 150 * mm});
        }
        {
            var Q0;
            Q0=makeQuery(id+"F8.opPattern","COPY",BODY,{"derivedFrom":makeQuery(id+"F4.opExtrude","SWEPT_BODY",BODY,{"disambiguationData":[OSD([sQuery(id+"F1.wireOp",EDGE,"E2"),sQuery(id+"F1.wireOp",EDGE,"E3"),sQuery(id+"F1.wireOp",EDGE,"E4"),sQuery(id+"F1.wireOp",EDGE,"E5"),sQuery(id+"F1.wireOp",EDGE,"E6")])]}),"instanceName":"1"});
            var Q1;
            Q1=makeQuery(id+"F8.opPattern","COPY",BODY,{"derivedFrom":makeQuery(id+"F5.opPattern","COPY",BODY,{"derivedFrom":makeQuery(id+"F4.opExtrude","SWEPT_BODY",BODY,{"disambiguationData":[OSD([sQuery(id+"F1.wireOp",EDGE,"E2"),sQuery(id+"F1.wireOp",EDGE,"E3"),sQuery(id+"F1.wireOp",EDGE,"E4"),sQuery(id+"F1.wireOp",EDGE,"E5"),sQuery(id+"F1.wireOp",EDGE,"E6")])]}),"instanceName":"34"}),"instanceName":"1"});
            var Q2;
            Q2=makeQuery(id+"F8.opPattern","COPY",BODY,{"derivedFrom":makeQuery(id+"F5.opPattern","COPY",BODY,{"derivedFrom":makeQuery(id+"F4.opExtrude","SWEPT_BODY",BODY,{"disambiguationData":[OSD([sQuery(id+"F1.wireOp",EDGE,"E2"),sQuery(id+"F1.wireOp",EDGE,"E3"),sQuery(id+"F1.wireOp",EDGE,"E4"),sQuery(id+"F1.wireOp",EDGE,"E5"),sQuery(id+"F1.wireOp",EDGE,"E6")])]}),"instanceName":"32"}),"instanceName":"1"});
            var Q3;
            Q3=makeQuery(id+"F8.opPattern","COPY",BODY,{"derivedFrom":makeQuery(id+"F5.opPattern","COPY",BODY,{"derivedFrom":makeQuery(id+"F4.opExtrude","SWEPT_BODY",BODY,{"disambiguationData":[OSD([sQuery(id+"F1.wireOp",EDGE,"E2"),sQuery(id+"F1.wireOp",EDGE,"E3"),sQuery(id+"F1.wireOp",EDGE,"E4"),sQuery(id+"F1.wireOp",EDGE,"E5"),sQuery(id+"F1.wireOp",EDGE,"E6")])]}),"instanceName":"33"}),"instanceName":"1"});
            var Q4;
            Q4=makeQuery(id+"F8.opPattern","COPY",BODY,{"derivedFrom":makeQuery(id+"F5.opPattern","COPY",BODY,{"derivedFrom":makeQuery(id+"F4.opExtrude","SWEPT_BODY",BODY,{"disambiguationData":[OSD([sQuery(id+"F1.wireOp",EDGE,"E2"),sQuery(id+"F1.wireOp",EDGE,"E3"),sQuery(id+"F1.wireOp",EDGE,"E4"),sQuery(id+"F1.wireOp",EDGE,"E5"),sQuery(id+"F1.wireOp",EDGE,"E6")])]}),"instanceName":"35"}),"instanceName":"1"});
            var Q5;
            Q5=makeQuery(id+"F8.opPattern","COPY",BODY,{"derivedFrom":makeQuery(id+"F5.opPattern","COPY",BODY,{"derivedFrom":makeQuery(id+"F4.opExtrude","SWEPT_BODY",BODY,{"disambiguationData":[OSD([sQuery(id+"F1.wireOp",EDGE,"E2"),sQuery(id+"F1.wireOp",EDGE,"E3"),sQuery(id+"F1.wireOp",EDGE,"E4"),sQuery(id+"F1.wireOp",EDGE,"E5"),sQuery(id+"F1.wireOp",EDGE,"E6")])]}),"instanceName":"31"}),"instanceName":"1"});
            var Q6;
            Q6=makeQuery(id+"F8.opPattern","COPY",BODY,{"derivedFrom":makeQuery(id+"F5.opPattern","COPY",BODY,{"derivedFrom":makeQuery(id+"F4.opExtrude","SWEPT_BODY",BODY,{"disambiguationData":[OSD([sQuery(id+"F1.wireOp",EDGE,"E2"),sQuery(id+"F1.wireOp",EDGE,"E3"),sQuery(id+"F1.wireOp",EDGE,"E4"),sQuery(id+"F1.wireOp",EDGE,"E5"),sQuery(id+"F1.wireOp",EDGE,"E6")])]}),"instanceName":"30"}),"instanceName":"1"});
            var Q7;
            Q7=makeQuery(id+"F8.opPattern","COPY",BODY,{"derivedFrom":makeQuery(id+"F5.opPattern","COPY",BODY,{"derivedFrom":makeQuery(id+"F4.opExtrude","SWEPT_BODY",BODY,{"disambiguationData":[OSD([sQuery(id+"F1.wireOp",EDGE,"E2"),sQuery(id+"F1.wireOp",EDGE,"E3"),sQuery(id+"F1.wireOp",EDGE,"E4"),sQuery(id+"F1.wireOp",EDGE,"E5"),sQuery(id+"F1.wireOp",EDGE,"E6")])]}),"instanceName":"29"}),"instanceName":"1"});
            var Q8;
            Q8=makeQuery(id+"F8.opPattern","COPY",BODY,{"derivedFrom":makeQuery(id+"F5.opPattern","COPY",BODY,{"derivedFrom":makeQuery(id+"F4.opExtrude","SWEPT_BODY",BODY,{"disambiguationData":[OSD([sQuery(id+"F1.wireOp",EDGE,"E2"),sQuery(id+"F1.wireOp",EDGE,"E3"),sQuery(id+"F1.wireOp",EDGE,"E4"),sQuery(id+"F1.wireOp",EDGE,"E5"),sQuery(id+"F1.wireOp",EDGE,"E6")])]}),"instanceName":"28"}),"instanceName":"1"});
            var Q9;
            Q9=makeQuery(id+"F8.opPattern","COPY",BODY,{"derivedFrom":makeQuery(id+"F5.opPattern","COPY",BODY,{"derivedFrom":makeQuery(id+"F4.opExtrude","SWEPT_BODY",BODY,{"disambiguationData":[OSD([sQuery(id+"F1.wireOp",EDGE,"E2"),sQuery(id+"F1.wireOp",EDGE,"E3"),sQuery(id+"F1.wireOp",EDGE,"E4"),sQuery(id+"F1.wireOp",EDGE,"E5"),sQuery(id+"F1.wireOp",EDGE,"E6")])]}),"instanceName":"27"}),"instanceName":"1"});
            var Q10;
            Q10=makeQuery(id+"F8.opPattern","COPY",BODY,{"derivedFrom":makeQuery(id+"F5.opPattern","COPY",BODY,{"derivedFrom":makeQuery(id+"F4.opExtrude","SWEPT_BODY",BODY,{"disambiguationData":[OSD([sQuery(id+"F1.wireOp",EDGE,"E2"),sQuery(id+"F1.wireOp",EDGE,"E3"),sQuery(id+"F1.wireOp",EDGE,"E4"),sQuery(id+"F1.wireOp",EDGE,"E5"),sQuery(id+"F1.wireOp",EDGE,"E6")])]}),"instanceName":"26"}),"instanceName":"1"});
            var Q11;
            Q11=makeQuery(id+"F8.opPattern","COPY",BODY,{"derivedFrom":makeQuery(id+"F5.opPattern","COPY",BODY,{"derivedFrom":makeQuery(id+"F4.opExtrude","SWEPT_BODY",BODY,{"disambiguationData":[OSD([sQuery(id+"F1.wireOp",EDGE,"E2"),sQuery(id+"F1.wireOp",EDGE,"E3"),sQuery(id+"F1.wireOp",EDGE,"E4"),sQuery(id+"F1.wireOp",EDGE,"E5"),sQuery(id+"F1.wireOp",EDGE,"E6")])]}),"instanceName":"25"}),"instanceName":"1"});
            var Q12;
            Q12=makeQuery(id+"F8.opPattern","COPY",BODY,{"derivedFrom":makeQuery(id+"F5.opPattern","COPY",BODY,{"derivedFrom":makeQuery(id+"F4.opExtrude","SWEPT_BODY",BODY,{"disambiguationData":[OSD([sQuery(id+"F1.wireOp",EDGE,"E2"),sQuery(id+"F1.wireOp",EDGE,"E3"),sQuery(id+"F1.wireOp",EDGE,"E4"),sQuery(id+"F1.wireOp",EDGE,"E5"),sQuery(id+"F1.wireOp",EDGE,"E6")])]}),"instanceName":"24"}),"instanceName":"1"});
            var Q13;
            Q13=makeQuery(id+"F8.opPattern","COPY",BODY,{"derivedFrom":makeQuery(id+"F5.opPattern","COPY",BODY,{"derivedFrom":makeQuery(id+"F4.opExtrude","SWEPT_BODY",BODY,{"disambiguationData":[OSD([sQuery(id+"F1.wireOp",EDGE,"E2"),sQuery(id+"F1.wireOp",EDGE,"E3"),sQuery(id+"F1.wireOp",EDGE,"E4"),sQuery(id+"F1.wireOp",EDGE,"E5"),sQuery(id+"F1.wireOp",EDGE,"E6")])]}),"instanceName":"23"}),"instanceName":"1"});
            var Q14;
            Q14=makeQuery(id+"F8.opPattern","COPY",BODY,{"derivedFrom":makeQuery(id+"F5.opPattern","COPY",BODY,{"derivedFrom":makeQuery(id+"F4.opExtrude","SWEPT_BODY",BODY,{"disambiguationData":[OSD([sQuery(id+"F1.wireOp",EDGE,"E2"),sQuery(id+"F1.wireOp",EDGE,"E3"),sQuery(id+"F1.wireOp",EDGE,"E4"),sQuery(id+"F1.wireOp",EDGE,"E5"),sQuery(id+"F1.wireOp",EDGE,"E6")])]}),"instanceName":"21"}),"instanceName":"1"});
            var Q15;
            Q15=makeQuery(id+"F8.opPattern","COPY",BODY,{"derivedFrom":makeQuery(id+"F5.opPattern","COPY",BODY,{"derivedFrom":makeQuery(id+"F4.opExtrude","SWEPT_BODY",BODY,{"disambiguationData":[OSD([sQuery(id+"F1.wireOp",EDGE,"E2"),sQuery(id+"F1.wireOp",EDGE,"E3"),sQuery(id+"F1.wireOp",EDGE,"E4"),sQuery(id+"F1.wireOp",EDGE,"E5"),sQuery(id+"F1.wireOp",EDGE,"E6")])]}),"instanceName":"20"}),"instanceName":"1"});
            var Q16;
            Q16=makeQuery(id+"F8.opPattern","COPY",BODY,{"derivedFrom":makeQuery(id+"F5.opPattern","COPY",BODY,{"derivedFrom":makeQuery(id+"F4.opExtrude","SWEPT_BODY",BODY,{"disambiguationData":[OSD([sQuery(id+"F1.wireOp",EDGE,"E2"),sQuery(id+"F1.wireOp",EDGE,"E3"),sQuery(id+"F1.wireOp",EDGE,"E4"),sQuery(id+"F1.wireOp",EDGE,"E5"),sQuery(id+"F1.wireOp",EDGE,"E6")])]}),"instanceName":"19"}),"instanceName":"1"});
            var Q17;
            Q17=makeQuery(id+"F8.opPattern","COPY",BODY,{"derivedFrom":makeQuery(id+"F5.opPattern","COPY",BODY,{"derivedFrom":makeQuery(id+"F4.opExtrude","SWEPT_BODY",BODY,{"disambiguationData":[OSD([sQuery(id+"F1.wireOp",EDGE,"E2"),sQuery(id+"F1.wireOp",EDGE,"E3"),sQuery(id+"F1.wireOp",EDGE,"E4"),sQuery(id+"F1.wireOp",EDGE,"E5"),sQuery(id+"F1.wireOp",EDGE,"E6")])]}),"instanceName":"18"}),"instanceName":"1"});
            var Q18;
            Q18=makeQuery(id+"F8.opPattern","COPY",BODY,{"derivedFrom":makeQuery(id+"F5.opPattern","COPY",BODY,{"derivedFrom":makeQuery(id+"F4.opExtrude","SWEPT_BODY",BODY,{"disambiguationData":[OSD([sQuery(id+"F1.wireOp",EDGE,"E2"),sQuery(id+"F1.wireOp",EDGE,"E3"),sQuery(id+"F1.wireOp",EDGE,"E4"),sQuery(id+"F1.wireOp",EDGE,"E5"),sQuery(id+"F1.wireOp",EDGE,"E6")])]}),"instanceName":"13"}),"instanceName":"1"});
            var Q19;
            Q19=makeQuery(id+"F8.opPattern","COPY",BODY,{"derivedFrom":makeQuery(id+"F5.opPattern","COPY",BODY,{"derivedFrom":makeQuery(id+"F4.opExtrude","SWEPT_BODY",BODY,{"disambiguationData":[OSD([sQuery(id+"F1.wireOp",EDGE,"E2"),sQuery(id+"F1.wireOp",EDGE,"E3"),sQuery(id+"F1.wireOp",EDGE,"E4"),sQuery(id+"F1.wireOp",EDGE,"E5"),sQuery(id+"F1.wireOp",EDGE,"E6")])]}),"instanceName":"12"}),"instanceName":"1"});
            var Q20;
            Q20=makeQuery(id+"F8.opPattern","COPY",BODY,{"derivedFrom":makeQuery(id+"F5.opPattern","COPY",BODY,{"derivedFrom":makeQuery(id+"F4.opExtrude","SWEPT_BODY",BODY,{"disambiguationData":[OSD([sQuery(id+"F1.wireOp",EDGE,"E2"),sQuery(id+"F1.wireOp",EDGE,"E3"),sQuery(id+"F1.wireOp",EDGE,"E4"),sQuery(id+"F1.wireOp",EDGE,"E5"),sQuery(id+"F1.wireOp",EDGE,"E6")])]}),"instanceName":"10"}),"instanceName":"1"});
            var Q21;
            Q21=makeQuery(id+"F8.opPattern","COPY",BODY,{"derivedFrom":makeQuery(id+"F5.opPattern","COPY",BODY,{"derivedFrom":makeQuery(id+"F4.opExtrude","SWEPT_BODY",BODY,{"disambiguationData":[OSD([sQuery(id+"F1.wireOp",EDGE,"E2"),sQuery(id+"F1.wireOp",EDGE,"E3"),sQuery(id+"F1.wireOp",EDGE,"E4"),sQuery(id+"F1.wireOp",EDGE,"E5"),sQuery(id+"F1.wireOp",EDGE,"E6")])]}),"instanceName":"9"}),"instanceName":"1"});
            var Q22;
            Q22=makeQuery(id+"F8.opPattern","COPY",BODY,{"derivedFrom":makeQuery(id+"F5.opPattern","COPY",BODY,{"derivedFrom":makeQuery(id+"F4.opExtrude","SWEPT_BODY",BODY,{"disambiguationData":[OSD([sQuery(id+"F1.wireOp",EDGE,"E2"),sQuery(id+"F1.wireOp",EDGE,"E3"),sQuery(id+"F1.wireOp",EDGE,"E4"),sQuery(id+"F1.wireOp",EDGE,"E5"),sQuery(id+"F1.wireOp",EDGE,"E6")])]}),"instanceName":"3"}),"instanceName":"1"});
            var Q23;
            Q23=makeQuery(id+"F8.opPattern","COPY",BODY,{"derivedFrom":makeQuery(id+"F5.opPattern","COPY",BODY,{"derivedFrom":makeQuery(id+"F4.opExtrude","SWEPT_BODY",BODY,{"disambiguationData":[OSD([sQuery(id+"F1.wireOp",EDGE,"E2"),sQuery(id+"F1.wireOp",EDGE,"E3"),sQuery(id+"F1.wireOp",EDGE,"E4"),sQuery(id+"F1.wireOp",EDGE,"E5"),sQuery(id+"F1.wireOp",EDGE,"E6")])]}),"instanceName":"2"}),"instanceName":"1"});
            var Q24;
            Q24=makeQuery(id+"F8.opPattern","COPY",BODY,{"derivedFrom":makeQuery(id+"F5.opPattern","COPY",BODY,{"derivedFrom":makeQuery(id+"F4.opExtrude","SWEPT_BODY",BODY,{"disambiguationData":[OSD([sQuery(id+"F1.wireOp",EDGE,"E2"),sQuery(id+"F1.wireOp",EDGE,"E3"),sQuery(id+"F1.wireOp",EDGE,"E4"),sQuery(id+"F1.wireOp",EDGE,"E5"),sQuery(id+"F1.wireOp",EDGE,"E6")])]}),"instanceName":"1"}),"instanceName":"1"});
            var Q25;
            Q25=makeQuery(id+"F8.opPattern","COPY",BODY,{"derivedFrom":makeQuery(id+"F5.opPattern","COPY",BODY,{"derivedFrom":makeQuery(id+"F4.opExtrude","SWEPT_BODY",BODY,{"disambiguationData":[OSD([sQuery(id+"F1.wireOp",EDGE,"E2"),sQuery(id+"F1.wireOp",EDGE,"E3"),sQuery(id+"F1.wireOp",EDGE,"E4"),sQuery(id+"F1.wireOp",EDGE,"E5"),sQuery(id+"F1.wireOp",EDGE,"E6")])]}),"instanceName":"22"}),"instanceName":"1"});
            var Q26;
            Q26=makeQuery(id+"F8.opPattern","COPY",BODY,{"derivedFrom":makeQuery(id+"F5.opPattern","COPY",BODY,{"derivedFrom":makeQuery(id+"F4.opExtrude","SWEPT_BODY",BODY,{"disambiguationData":[OSD([sQuery(id+"F1.wireOp",EDGE,"E2"),sQuery(id+"F1.wireOp",EDGE,"E3"),sQuery(id+"F1.wireOp",EDGE,"E4"),sQuery(id+"F1.wireOp",EDGE,"E5"),sQuery(id+"F1.wireOp",EDGE,"E6")])]}),"instanceName":"17"}),"instanceName":"1"});
            var Q27;
            Q27=makeQuery(id+"F8.opPattern","COPY",BODY,{"derivedFrom":makeQuery(id+"F5.opPattern","COPY",BODY,{"derivedFrom":makeQuery(id+"F4.opExtrude","SWEPT_BODY",BODY,{"disambiguationData":[OSD([sQuery(id+"F1.wireOp",EDGE,"E2"),sQuery(id+"F1.wireOp",EDGE,"E3"),sQuery(id+"F1.wireOp",EDGE,"E4"),sQuery(id+"F1.wireOp",EDGE,"E5"),sQuery(id+"F1.wireOp",EDGE,"E6")])]}),"instanceName":"16"}),"instanceName":"1"});
            var Q28;
            Q28=makeQuery(id+"F8.opPattern","COPY",BODY,{"derivedFrom":makeQuery(id+"F5.opPattern","COPY",BODY,{"derivedFrom":makeQuery(id+"F4.opExtrude","SWEPT_BODY",BODY,{"disambiguationData":[OSD([sQuery(id+"F1.wireOp",EDGE,"E2"),sQuery(id+"F1.wireOp",EDGE,"E3"),sQuery(id+"F1.wireOp",EDGE,"E4"),sQuery(id+"F1.wireOp",EDGE,"E5"),sQuery(id+"F1.wireOp",EDGE,"E6")])]}),"instanceName":"15"}),"instanceName":"1"});
            var Q29;
            Q29=makeQuery(id+"F8.opPattern","COPY",BODY,{"derivedFrom":makeQuery(id+"F5.opPattern","COPY",BODY,{"derivedFrom":makeQuery(id+"F4.opExtrude","SWEPT_BODY",BODY,{"disambiguationData":[OSD([sQuery(id+"F1.wireOp",EDGE,"E2"),sQuery(id+"F1.wireOp",EDGE,"E3"),sQuery(id+"F1.wireOp",EDGE,"E4"),sQuery(id+"F1.wireOp",EDGE,"E5"),sQuery(id+"F1.wireOp",EDGE,"E6")])]}),"instanceName":"14"}),"instanceName":"1"});
            var Q30;
            Q30=makeQuery(id+"F8.opPattern","COPY",BODY,{"derivedFrom":makeQuery(id+"F5.opPattern","COPY",BODY,{"derivedFrom":makeQuery(id+"F4.opExtrude","SWEPT_BODY",BODY,{"disambiguationData":[OSD([sQuery(id+"F1.wireOp",EDGE,"E2"),sQuery(id+"F1.wireOp",EDGE,"E3"),sQuery(id+"F1.wireOp",EDGE,"E4"),sQuery(id+"F1.wireOp",EDGE,"E5"),sQuery(id+"F1.wireOp",EDGE,"E6")])]}),"instanceName":"11"}),"instanceName":"1"});
            var Q31;
            Q31=makeQuery(id+"F8.opPattern","COPY",BODY,{"derivedFrom":makeQuery(id+"F5.opPattern","COPY",BODY,{"derivedFrom":makeQuery(id+"F4.opExtrude","SWEPT_BODY",BODY,{"disambiguationData":[OSD([sQuery(id+"F1.wireOp",EDGE,"E2"),sQuery(id+"F1.wireOp",EDGE,"E3"),sQuery(id+"F1.wireOp",EDGE,"E4"),sQuery(id+"F1.wireOp",EDGE,"E5"),sQuery(id+"F1.wireOp",EDGE,"E6")])]}),"instanceName":"8"}),"instanceName":"1"});
            var Q32;
            Q32=makeQuery(id+"F8.opPattern","COPY",BODY,{"derivedFrom":makeQuery(id+"F5.opPattern","COPY",BODY,{"derivedFrom":makeQuery(id+"F4.opExtrude","SWEPT_BODY",BODY,{"disambiguationData":[OSD([sQuery(id+"F1.wireOp",EDGE,"E2"),sQuery(id+"F1.wireOp",EDGE,"E3"),sQuery(id+"F1.wireOp",EDGE,"E4"),sQuery(id+"F1.wireOp",EDGE,"E5"),sQuery(id+"F1.wireOp",EDGE,"E6")])]}),"instanceName":"7"}),"instanceName":"1"});
            var Q33;
            Q33=makeQuery(id+"F8.opPattern","COPY",BODY,{"derivedFrom":makeQuery(id+"F5.opPattern","COPY",BODY,{"derivedFrom":makeQuery(id+"F4.opExtrude","SWEPT_BODY",BODY,{"disambiguationData":[OSD([sQuery(id+"F1.wireOp",EDGE,"E2"),sQuery(id+"F1.wireOp",EDGE,"E3"),sQuery(id+"F1.wireOp",EDGE,"E4"),sQuery(id+"F1.wireOp",EDGE,"E5"),sQuery(id+"F1.wireOp",EDGE,"E6")])]}),"instanceName":"6"}),"instanceName":"1"});
            var Q34;
            Q34=makeQuery(id+"F8.opPattern","COPY",BODY,{"derivedFrom":makeQuery(id+"F5.opPattern","COPY",BODY,{"derivedFrom":makeQuery(id+"F4.opExtrude","SWEPT_BODY",BODY,{"disambiguationData":[OSD([sQuery(id+"F1.wireOp",EDGE,"E2"),sQuery(id+"F1.wireOp",EDGE,"E3"),sQuery(id+"F1.wireOp",EDGE,"E4"),sQuery(id+"F1.wireOp",EDGE,"E5"),sQuery(id+"F1.wireOp",EDGE,"E6")])]}),"instanceName":"5"}),"instanceName":"1"});
            var Q35;
            Q35=makeQuery(id+"F8.opPattern","COPY",BODY,{"derivedFrom":makeQuery(id+"F5.opPattern","COPY",BODY,{"derivedFrom":makeQuery(id+"F4.opExtrude","SWEPT_BODY",BODY,{"disambiguationData":[OSD([sQuery(id+"F1.wireOp",EDGE,"E2"),sQuery(id+"F1.wireOp",EDGE,"E3"),sQuery(id+"F1.wireOp",EDGE,"E4"),sQuery(id+"F1.wireOp",EDGE,"E5"),sQuery(id+"F1.wireOp",EDGE,"E6")])]}),"instanceName":"4"}),"instanceName":"1"});
            var Q36;
            Q36=makeQuery(id+"F5.opPattern","COPY",BODY,{"derivedFrom":makeQuery(id+"F4.opExtrude","SWEPT_BODY",BODY,{"disambiguationData":[OSD([sQuery(id+"F1.wireOp",EDGE,"E2"),sQuery(id+"F1.wireOp",EDGE,"E3"),sQuery(id+"F1.wireOp",EDGE,"E4"),sQuery(id+"F1.wireOp",EDGE,"E5"),sQuery(id+"F1.wireOp",EDGE,"E6")])]}),"instanceName":"32"});
            var Q37;
            Q37=makeQuery(id+"F5.opPattern","COPY",BODY,{"derivedFrom":makeQuery(id+"F4.opExtrude","SWEPT_BODY",BODY,{"disambiguationData":[OSD([sQuery(id+"F1.wireOp",EDGE,"E2"),sQuery(id+"F1.wireOp",EDGE,"E3"),sQuery(id+"F1.wireOp",EDGE,"E4"),sQuery(id+"F1.wireOp",EDGE,"E5"),sQuery(id+"F1.wireOp",EDGE,"E6")])]}),"instanceName":"30"});
            var Q38;
            Q38=makeQuery(id+"F5.opPattern","COPY",BODY,{"derivedFrom":makeQuery(id+"F4.opExtrude","SWEPT_BODY",BODY,{"disambiguationData":[OSD([sQuery(id+"F1.wireOp",EDGE,"E2"),sQuery(id+"F1.wireOp",EDGE,"E3"),sQuery(id+"F1.wireOp",EDGE,"E4"),sQuery(id+"F1.wireOp",EDGE,"E5"),sQuery(id+"F1.wireOp",EDGE,"E6")])]}),"instanceName":"35"});
            var Q39;
            Q39=makeQuery(id+"F5.opPattern","COPY",BODY,{"derivedFrom":makeQuery(id+"F4.opExtrude","SWEPT_BODY",BODY,{"disambiguationData":[OSD([sQuery(id+"F1.wireOp",EDGE,"E2"),sQuery(id+"F1.wireOp",EDGE,"E3"),sQuery(id+"F1.wireOp",EDGE,"E4"),sQuery(id+"F1.wireOp",EDGE,"E5"),sQuery(id+"F1.wireOp",EDGE,"E6")])]}),"instanceName":"26"});
            var Q40;
            Q40=makeQuery(id+"F5.opPattern","COPY",BODY,{"derivedFrom":makeQuery(id+"F4.opExtrude","SWEPT_BODY",BODY,{"disambiguationData":[OSD([sQuery(id+"F1.wireOp",EDGE,"E2"),sQuery(id+"F1.wireOp",EDGE,"E3"),sQuery(id+"F1.wireOp",EDGE,"E4"),sQuery(id+"F1.wireOp",EDGE,"E5"),sQuery(id+"F1.wireOp",EDGE,"E6")])]}),"instanceName":"33"});
            var Q41;
            Q41=makeQuery(id+"F5.opPattern","COPY",BODY,{"derivedFrom":makeQuery(id+"F4.opExtrude","SWEPT_BODY",BODY,{"disambiguationData":[OSD([sQuery(id+"F1.wireOp",EDGE,"E2"),sQuery(id+"F1.wireOp",EDGE,"E3"),sQuery(id+"F1.wireOp",EDGE,"E4"),sQuery(id+"F1.wireOp",EDGE,"E5"),sQuery(id+"F1.wireOp",EDGE,"E6")])]}),"instanceName":"18"});
            var Q42;
            Q42=makeQuery(id+"F5.opPattern","COPY",BODY,{"derivedFrom":makeQuery(id+"F4.opExtrude","SWEPT_BODY",BODY,{"disambiguationData":[OSD([sQuery(id+"F1.wireOp",EDGE,"E2"),sQuery(id+"F1.wireOp",EDGE,"E3"),sQuery(id+"F1.wireOp",EDGE,"E4"),sQuery(id+"F1.wireOp",EDGE,"E5"),sQuery(id+"F1.wireOp",EDGE,"E6")])]}),"instanceName":"24"});
            var Q43;
            Q43=makeQuery(id+"F5.opPattern","COPY",BODY,{"derivedFrom":makeQuery(id+"F4.opExtrude","SWEPT_BODY",BODY,{"disambiguationData":[OSD([sQuery(id+"F1.wireOp",EDGE,"E2"),sQuery(id+"F1.wireOp",EDGE,"E3"),sQuery(id+"F1.wireOp",EDGE,"E4"),sQuery(id+"F1.wireOp",EDGE,"E5"),sQuery(id+"F1.wireOp",EDGE,"E6")])]}),"instanceName":"31"});
            var Q44;
            Q44=makeQuery(id+"F5.opPattern","COPY",BODY,{"derivedFrom":makeQuery(id+"F4.opExtrude","SWEPT_BODY",BODY,{"disambiguationData":[OSD([sQuery(id+"F1.wireOp",EDGE,"E2"),sQuery(id+"F1.wireOp",EDGE,"E3"),sQuery(id+"F1.wireOp",EDGE,"E4"),sQuery(id+"F1.wireOp",EDGE,"E5"),sQuery(id+"F1.wireOp",EDGE,"E6")])]}),"instanceName":"19"});
            var Q45;
            Q45=makeQuery(id+"F5.opPattern","COPY",BODY,{"derivedFrom":makeQuery(id+"F4.opExtrude","SWEPT_BODY",BODY,{"disambiguationData":[OSD([sQuery(id+"F1.wireOp",EDGE,"E2"),sQuery(id+"F1.wireOp",EDGE,"E3"),sQuery(id+"F1.wireOp",EDGE,"E4"),sQuery(id+"F1.wireOp",EDGE,"E5"),sQuery(id+"F1.wireOp",EDGE,"E6")])]}),"instanceName":"21"});
            var Q46;
            Q46=makeQuery(id+"F5.opPattern","COPY",BODY,{"derivedFrom":makeQuery(id+"F4.opExtrude","SWEPT_BODY",BODY,{"disambiguationData":[OSD([sQuery(id+"F1.wireOp",EDGE,"E2"),sQuery(id+"F1.wireOp",EDGE,"E3"),sQuery(id+"F1.wireOp",EDGE,"E4"),sQuery(id+"F1.wireOp",EDGE,"E5"),sQuery(id+"F1.wireOp",EDGE,"E6")])]}),"instanceName":"23"});
            var Q47;
            Q47=makeQuery(id+"F4.opExtrude","SWEPT_BODY",BODY,{"disambiguationData":[OSD([sQuery(id+"F1.wireOp",EDGE,"E2"),sQuery(id+"F1.wireOp",EDGE,"E3"),sQuery(id+"F1.wireOp",EDGE,"E4"),sQuery(id+"F1.wireOp",EDGE,"E5"),sQuery(id+"F1.wireOp",EDGE,"E6")])]});
            var Q48;
            Q48=makeQuery(id+"F5.opPattern","COPY",BODY,{"derivedFrom":makeQuery(id+"F4.opExtrude","SWEPT_BODY",BODY,{"disambiguationData":[OSD([sQuery(id+"F1.wireOp",EDGE,"E2"),sQuery(id+"F1.wireOp",EDGE,"E3"),sQuery(id+"F1.wireOp",EDGE,"E4"),sQuery(id+"F1.wireOp",EDGE,"E5"),sQuery(id+"F1.wireOp",EDGE,"E6")])]}),"instanceName":"28"});
            var Q49;
            Q49=makeQuery(id+"F5.opPattern","COPY",BODY,{"derivedFrom":makeQuery(id+"F4.opExtrude","SWEPT_BODY",BODY,{"disambiguationData":[OSD([sQuery(id+"F1.wireOp",EDGE,"E2"),sQuery(id+"F1.wireOp",EDGE,"E3"),sQuery(id+"F1.wireOp",EDGE,"E4"),sQuery(id+"F1.wireOp",EDGE,"E5"),sQuery(id+"F1.wireOp",EDGE,"E6")])]}),"instanceName":"25"});
            var Q50;
            Q50=makeQuery(id+"F5.opPattern","COPY",BODY,{"derivedFrom":makeQuery(id+"F4.opExtrude","SWEPT_BODY",BODY,{"disambiguationData":[OSD([sQuery(id+"F1.wireOp",EDGE,"E2"),sQuery(id+"F1.wireOp",EDGE,"E3"),sQuery(id+"F1.wireOp",EDGE,"E4"),sQuery(id+"F1.wireOp",EDGE,"E5"),sQuery(id+"F1.wireOp",EDGE,"E6")])]}),"instanceName":"29"});
            var Q51;
            Q51=makeQuery(id+"F5.opPattern","COPY",BODY,{"derivedFrom":makeQuery(id+"F4.opExtrude","SWEPT_BODY",BODY,{"disambiguationData":[OSD([sQuery(id+"F1.wireOp",EDGE,"E2"),sQuery(id+"F1.wireOp",EDGE,"E3"),sQuery(id+"F1.wireOp",EDGE,"E4"),sQuery(id+"F1.wireOp",EDGE,"E5"),sQuery(id+"F1.wireOp",EDGE,"E6")])]}),"instanceName":"20"});
            var Q52;
            Q52=makeQuery(id+"F5.opPattern","COPY",BODY,{"derivedFrom":makeQuery(id+"F4.opExtrude","SWEPT_BODY",BODY,{"disambiguationData":[OSD([sQuery(id+"F1.wireOp",EDGE,"E2"),sQuery(id+"F1.wireOp",EDGE,"E3"),sQuery(id+"F1.wireOp",EDGE,"E4"),sQuery(id+"F1.wireOp",EDGE,"E5"),sQuery(id+"F1.wireOp",EDGE,"E6")])]}),"instanceName":"22"});
            var Q53;
            Q53=makeQuery(id+"F5.opPattern","COPY",BODY,{"derivedFrom":makeQuery(id+"F4.opExtrude","SWEPT_BODY",BODY,{"disambiguationData":[OSD([sQuery(id+"F1.wireOp",EDGE,"E2"),sQuery(id+"F1.wireOp",EDGE,"E3"),sQuery(id+"F1.wireOp",EDGE,"E4"),sQuery(id+"F1.wireOp",EDGE,"E5"),sQuery(id+"F1.wireOp",EDGE,"E6")])]}),"instanceName":"27"});
            var Q54;
            Q54=makeQuery(id+"F5.opPattern","COPY",BODY,{"derivedFrom":makeQuery(id+"F4.opExtrude","SWEPT_BODY",BODY,{"disambiguationData":[OSD([sQuery(id+"F1.wireOp",EDGE,"E2"),sQuery(id+"F1.wireOp",EDGE,"E3"),sQuery(id+"F1.wireOp",EDGE,"E4"),sQuery(id+"F1.wireOp",EDGE,"E5"),sQuery(id+"F1.wireOp",EDGE,"E6")])]}),"instanceName":"34"});
            var Q55;
            Q55=qCreatedBy(id+"F13.planeOp",FACE);
            mirror(context, id + "F14", {"entities" : qUnion([Q0, Q1, Q2, Q3, Q4, Q5, Q6, Q7, Q8, Q9, Q10, Q11, Q12, Q13, Q14, Q15, Q16, Q17, Q18, Q19, Q20, Q21, Q22, Q23, Q24, Q25, Q26, Q27, Q28, Q29, Q30, Q31, Q32, Q33, Q34, Q35, Q36, Q37, Q38, Q39, Q40, Q41, Q42, Q43, Q44, Q45, Q46, Q47, Q48, Q49, Q50, Q51, Q52, Q53, Q54]), "mirrorPlane" : qUnion([Q55])});
        }
        {
            var Q0;
            Q0=makeQuery(id+"F14.opPattern","COPY",BODY,{"derivedFrom":makeQuery(id+"F5.opPattern","COPY",BODY,{"derivedFrom":makeQuery(id+"F4.opExtrude","SWEPT_BODY",BODY,{"disambiguationData":[OSD([sQuery(id+"F1.wireOp",EDGE,"E2"),sQuery(id+"F1.wireOp",EDGE,"E3"),sQuery(id+"F1.wireOp",EDGE,"E4"),sQuery(id+"F1.wireOp",EDGE,"E5"),sQuery(id+"F1.wireOp",EDGE,"E6")])]}),"instanceName":"34"}),"instanceName":"1"});
            var Q1;
            Q1=makeQuery(id+"F14.opPattern","COPY",BODY,{"derivedFrom":makeQuery(id+"F5.opPattern","COPY",BODY,{"derivedFrom":makeQuery(id+"F4.opExtrude","SWEPT_BODY",BODY,{"disambiguationData":[OSD([sQuery(id+"F1.wireOp",EDGE,"E2"),sQuery(id+"F1.wireOp",EDGE,"E3"),sQuery(id+"F1.wireOp",EDGE,"E4"),sQuery(id+"F1.wireOp",EDGE,"E5"),sQuery(id+"F1.wireOp",EDGE,"E6")])]}),"instanceName":"35"}),"instanceName":"1"});
            var Q2;
            Q2=makeQuery(id+"F14.opPattern","COPY",BODY,{"derivedFrom":makeQuery(id+"F5.opPattern","COPY",BODY,{"derivedFrom":makeQuery(id+"F4.opExtrude","SWEPT_BODY",BODY,{"disambiguationData":[OSD([sQuery(id+"F1.wireOp",EDGE,"E2"),sQuery(id+"F1.wireOp",EDGE,"E3"),sQuery(id+"F1.wireOp",EDGE,"E4"),sQuery(id+"F1.wireOp",EDGE,"E5"),sQuery(id+"F1.wireOp",EDGE,"E6")])]}),"instanceName":"33"}),"instanceName":"1"});
            var Q3;
            Q3=makeQuery(id+"F14.opPattern","COPY",BODY,{"derivedFrom":makeQuery(id+"F5.opPattern","COPY",BODY,{"derivedFrom":makeQuery(id+"F4.opExtrude","SWEPT_BODY",BODY,{"disambiguationData":[OSD([sQuery(id+"F1.wireOp",EDGE,"E2"),sQuery(id+"F1.wireOp",EDGE,"E3"),sQuery(id+"F1.wireOp",EDGE,"E4"),sQuery(id+"F1.wireOp",EDGE,"E5"),sQuery(id+"F1.wireOp",EDGE,"E6")])]}),"instanceName":"32"}),"instanceName":"1"});
            var Q4;
            Q4=makeQuery(id+"F14.opPattern","COPY",BODY,{"derivedFrom":makeQuery(id+"F5.opPattern","COPY",BODY,{"derivedFrom":makeQuery(id+"F4.opExtrude","SWEPT_BODY",BODY,{"disambiguationData":[OSD([sQuery(id+"F1.wireOp",EDGE,"E2"),sQuery(id+"F1.wireOp",EDGE,"E3"),sQuery(id+"F1.wireOp",EDGE,"E4"),sQuery(id+"F1.wireOp",EDGE,"E5"),sQuery(id+"F1.wireOp",EDGE,"E6")])]}),"instanceName":"31"}),"instanceName":"1"});
            var Q5;
            Q5=makeQuery(id+"F14.opPattern","COPY",BODY,{"derivedFrom":makeQuery(id+"F5.opPattern","COPY",BODY,{"derivedFrom":makeQuery(id+"F4.opExtrude","SWEPT_BODY",BODY,{"disambiguationData":[OSD([sQuery(id+"F1.wireOp",EDGE,"E2"),sQuery(id+"F1.wireOp",EDGE,"E3"),sQuery(id+"F1.wireOp",EDGE,"E4"),sQuery(id+"F1.wireOp",EDGE,"E5"),sQuery(id+"F1.wireOp",EDGE,"E6")])]}),"instanceName":"30"}),"instanceName":"1"});
            var Q6;
            Q6=makeQuery(id+"F14.opPattern","COPY",BODY,{"derivedFrom":makeQuery(id+"F5.opPattern","COPY",BODY,{"derivedFrom":makeQuery(id+"F4.opExtrude","SWEPT_BODY",BODY,{"disambiguationData":[OSD([sQuery(id+"F1.wireOp",EDGE,"E2"),sQuery(id+"F1.wireOp",EDGE,"E3"),sQuery(id+"F1.wireOp",EDGE,"E4"),sQuery(id+"F1.wireOp",EDGE,"E5"),sQuery(id+"F1.wireOp",EDGE,"E6")])]}),"instanceName":"29"}),"instanceName":"1"});
            var Q7;
            Q7=makeQuery(id+"F14.opPattern","COPY",BODY,{"derivedFrom":makeQuery(id+"F5.opPattern","COPY",BODY,{"derivedFrom":makeQuery(id+"F4.opExtrude","SWEPT_BODY",BODY,{"disambiguationData":[OSD([sQuery(id+"F1.wireOp",EDGE,"E2"),sQuery(id+"F1.wireOp",EDGE,"E3"),sQuery(id+"F1.wireOp",EDGE,"E4"),sQuery(id+"F1.wireOp",EDGE,"E5"),sQuery(id+"F1.wireOp",EDGE,"E6")])]}),"instanceName":"28"}),"instanceName":"1"});
            var Q8;
            Q8=makeQuery(id+"F14.opPattern","COPY",BODY,{"derivedFrom":makeQuery(id+"F5.opPattern","COPY",BODY,{"derivedFrom":makeQuery(id+"F4.opExtrude","SWEPT_BODY",BODY,{"disambiguationData":[OSD([sQuery(id+"F1.wireOp",EDGE,"E2"),sQuery(id+"F1.wireOp",EDGE,"E3"),sQuery(id+"F1.wireOp",EDGE,"E4"),sQuery(id+"F1.wireOp",EDGE,"E5"),sQuery(id+"F1.wireOp",EDGE,"E6")])]}),"instanceName":"27"}),"instanceName":"1"});
            var Q9;
            Q9=makeQuery(id+"F14.opPattern","COPY",BODY,{"derivedFrom":makeQuery(id+"F5.opPattern","COPY",BODY,{"derivedFrom":makeQuery(id+"F4.opExtrude","SWEPT_BODY",BODY,{"disambiguationData":[OSD([sQuery(id+"F1.wireOp",EDGE,"E2"),sQuery(id+"F1.wireOp",EDGE,"E3"),sQuery(id+"F1.wireOp",EDGE,"E4"),sQuery(id+"F1.wireOp",EDGE,"E5"),sQuery(id+"F1.wireOp",EDGE,"E6")])]}),"instanceName":"26"}),"instanceName":"1"});
            var Q10;
            Q10=makeQuery(id+"F14.opPattern","COPY",BODY,{"derivedFrom":makeQuery(id+"F5.opPattern","COPY",BODY,{"derivedFrom":makeQuery(id+"F4.opExtrude","SWEPT_BODY",BODY,{"disambiguationData":[OSD([sQuery(id+"F1.wireOp",EDGE,"E2"),sQuery(id+"F1.wireOp",EDGE,"E3"),sQuery(id+"F1.wireOp",EDGE,"E4"),sQuery(id+"F1.wireOp",EDGE,"E5"),sQuery(id+"F1.wireOp",EDGE,"E6")])]}),"instanceName":"25"}),"instanceName":"1"});
            var Q11;
            Q11=makeQuery(id+"F14.opPattern","COPY",BODY,{"derivedFrom":makeQuery(id+"F5.opPattern","COPY",BODY,{"derivedFrom":makeQuery(id+"F4.opExtrude","SWEPT_BODY",BODY,{"disambiguationData":[OSD([sQuery(id+"F1.wireOp",EDGE,"E2"),sQuery(id+"F1.wireOp",EDGE,"E3"),sQuery(id+"F1.wireOp",EDGE,"E4"),sQuery(id+"F1.wireOp",EDGE,"E5"),sQuery(id+"F1.wireOp",EDGE,"E6")])]}),"instanceName":"24"}),"instanceName":"1"});
            var Q12;
            Q12=makeQuery(id+"F14.opPattern","COPY",BODY,{"derivedFrom":makeQuery(id+"F5.opPattern","COPY",BODY,{"derivedFrom":makeQuery(id+"F4.opExtrude","SWEPT_BODY",BODY,{"disambiguationData":[OSD([sQuery(id+"F1.wireOp",EDGE,"E2"),sQuery(id+"F1.wireOp",EDGE,"E3"),sQuery(id+"F1.wireOp",EDGE,"E4"),sQuery(id+"F1.wireOp",EDGE,"E5"),sQuery(id+"F1.wireOp",EDGE,"E6")])]}),"instanceName":"23"}),"instanceName":"1"});
            var Q13;
            Q13=makeQuery(id+"F14.opPattern","COPY",BODY,{"derivedFrom":makeQuery(id+"F5.opPattern","COPY",BODY,{"derivedFrom":makeQuery(id+"F4.opExtrude","SWEPT_BODY",BODY,{"disambiguationData":[OSD([sQuery(id+"F1.wireOp",EDGE,"E2"),sQuery(id+"F1.wireOp",EDGE,"E3"),sQuery(id+"F1.wireOp",EDGE,"E4"),sQuery(id+"F1.wireOp",EDGE,"E5"),sQuery(id+"F1.wireOp",EDGE,"E6")])]}),"instanceName":"22"}),"instanceName":"1"});
            var Q14;
            Q14=makeQuery(id+"F14.opPattern","COPY",BODY,{"derivedFrom":makeQuery(id+"F5.opPattern","COPY",BODY,{"derivedFrom":makeQuery(id+"F4.opExtrude","SWEPT_BODY",BODY,{"disambiguationData":[OSD([sQuery(id+"F1.wireOp",EDGE,"E2"),sQuery(id+"F1.wireOp",EDGE,"E3"),sQuery(id+"F1.wireOp",EDGE,"E4"),sQuery(id+"F1.wireOp",EDGE,"E5"),sQuery(id+"F1.wireOp",EDGE,"E6")])]}),"instanceName":"21"}),"instanceName":"1"});
            var Q15;
            Q15=makeQuery(id+"F14.opPattern","COPY",BODY,{"derivedFrom":makeQuery(id+"F5.opPattern","COPY",BODY,{"derivedFrom":makeQuery(id+"F4.opExtrude","SWEPT_BODY",BODY,{"disambiguationData":[OSD([sQuery(id+"F1.wireOp",EDGE,"E2"),sQuery(id+"F1.wireOp",EDGE,"E3"),sQuery(id+"F1.wireOp",EDGE,"E4"),sQuery(id+"F1.wireOp",EDGE,"E5"),sQuery(id+"F1.wireOp",EDGE,"E6")])]}),"instanceName":"20"}),"instanceName":"1"});
            var Q16;
            Q16=makeQuery(id+"F14.opPattern","COPY",BODY,{"derivedFrom":makeQuery(id+"F5.opPattern","COPY",BODY,{"derivedFrom":makeQuery(id+"F4.opExtrude","SWEPT_BODY",BODY,{"disambiguationData":[OSD([sQuery(id+"F1.wireOp",EDGE,"E2"),sQuery(id+"F1.wireOp",EDGE,"E3"),sQuery(id+"F1.wireOp",EDGE,"E4"),sQuery(id+"F1.wireOp",EDGE,"E5"),sQuery(id+"F1.wireOp",EDGE,"E6")])]}),"instanceName":"19"}),"instanceName":"1"});
            var Q17;
            Q17=makeQuery(id+"F14.opPattern","COPY",BODY,{"derivedFrom":makeQuery(id+"F5.opPattern","COPY",BODY,{"derivedFrom":makeQuery(id+"F4.opExtrude","SWEPT_BODY",BODY,{"disambiguationData":[OSD([sQuery(id+"F1.wireOp",EDGE,"E2"),sQuery(id+"F1.wireOp",EDGE,"E3"),sQuery(id+"F1.wireOp",EDGE,"E4"),sQuery(id+"F1.wireOp",EDGE,"E5"),sQuery(id+"F1.wireOp",EDGE,"E6")])]}),"instanceName":"18"}),"instanceName":"1"});
            var Q18;
            Q18=makeQuery(id+"F14.opPattern","COPY",BODY,{"derivedFrom":makeQuery(id+"F4.opExtrude","SWEPT_BODY",BODY,{"disambiguationData":[OSD([sQuery(id+"F1.wireOp",EDGE,"E2"),sQuery(id+"F1.wireOp",EDGE,"E3"),sQuery(id+"F1.wireOp",EDGE,"E4"),sQuery(id+"F1.wireOp",EDGE,"E5"),sQuery(id+"F1.wireOp",EDGE,"E6")])]}),"instanceName":"1"});
            var Q19;
            Q19=qCreatedBy(makeId("Top.planeOp"),FACE);
            mirror(context, id + "F15", {"entities" : qUnion([Q0, Q1, Q2, Q3, Q4, Q5, Q6, Q7, Q8, Q9, Q10, Q11, Q12, Q13, Q14, Q15, Q16, Q17, Q18]), "mirrorPlane" : qUnion([Q19])});
        }
        {
            var Q0;
            Q0=qCreatedBy(makeId("Right.planeOp"),FACE);
            var Q1;
            Q1=makeQuery(id+"F14.opPattern","COPY",VERTEX,{"derivedFrom":makeQuery(id+"F5.opPattern","COPY",VERTEX,{"derivedFrom":makeQuery(id+"F4.opExtrude","CAP_VERTEX",VERTEX,{"disambiguationData":[OSD([sQuery(id+"F1.wireOp",EDGE,"E3"),sQuery(id+"F1.wireOp",EDGE,"E4")])],"isStart":false}),"instanceName":"25"}),"instanceName":"1"});
            cPlane(context, id + "F16", {"entities" : qUnion([Q0, Q1]), "cplaneType" : CPlaneType.PLANE_POINT, "offset" : 25 * mm, "width" : 150 * mm, "height" : 150 * mm});
        }
        {
            var Q0;
            Q0=qCreatedBy(id+"F16.planeOp",FACE);
            cPlane(context, id + "F17", {"entities" : qUnion([Q0]), "cplaneType" : CPlaneType.OFFSET, "offset" : 10 * mm, "oppositeDirection" : true, "width" : 150 * mm, "height" : 150 * mm});
        }
        {
            var Q0;
            Q0=qCreatedBy(id+"F17.planeOp",FACE);
            var sketch = newSketch(context, id + "F18", { "sketchPlane" : qUnion([Q0])});
            skLineSegment(sketch, "E9", {"start": v(57.23, 0) * mm, "end": v(57.23, 4.48) * mm});
            skLineSegment(sketch, "E10", {"start": v(57.23, 4.48) * mm, "end": v(59.23, 4.48) * mm});
            skLineSegment(sketch, "E11", {"start": v(59.23, 4.48) * mm, "end": v(59.23, -4.44) * mm});
            skLineSegment(sketch, "E12", {"start": v(59.23, -4.44) * mm, "end": v(57.27, -4.44) * mm});
            skLineSegment(sketch, "E13", {"start": v(57.27, -4.44) * mm, "end": v(57.23, 0) * mm});
            skSolve(sketch);
        }
        {
            var Q0;
            Q0 = qSketchRegion(id + "F18", true);
            extrude(context, id + "F19", {"entities" : qUnion([Q0]), "oppositeDirection" : true, "depth" : 550 * mm, "offsetDistance" : 25 * mm});
        }
        {
            var Q0;
            Q0=makeQuery(id+"F19.opExtrude","SWEPT_BODY",BODY,{"disambiguationData":[OSD([sQuery(id+"F18.wireOp",EDGE,"E9"),sQuery(id+"F18.wireOp",EDGE,"E10"),sQuery(id+"F18.wireOp",EDGE,"E11"),sQuery(id+"F18.wireOp",EDGE,"E12"),sQuery(id+"F18.wireOp",EDGE,"E13")])]});
            var Q1;
            Q1=sQuery(id+"F6.wireOp",EDGE,"E8");
            circularPattern(context, id + "F20", {"entities" : qUnion([Q0]), "axis" : qUnion([Q1]), "angle" : 360 * degree, "instanceCount" : 36, "equalSpace" : true});
        }
        {
            var Q0;
            Q0=qCreatedBy(makeId("Right.planeOp"),FACE);
            var sketch = newSketch(context, id + "F21", { "sketchPlane" : qUnion([Q0])});
            skCircle(sketch, "E14", {"center": v(0.1, 0.15) * mm, "radius": 60.49 * mm});
            skCircle(sketch, "E15", {"center": v(0.1, 0.15) * mm, "radius": 61.89 * mm});
            skSolve(sketch);
        }
        {
            var Q0;
            Q0 = qSketchRegion(id + "F21", true);
            extrude(context, id + "F22", {"entities" : qUnion([Q0]), "endBound" : BoundingType.SYMMETRIC, "depth" : 9144 * mm, "offsetDistance" : 25 * mm});
        }
    });
